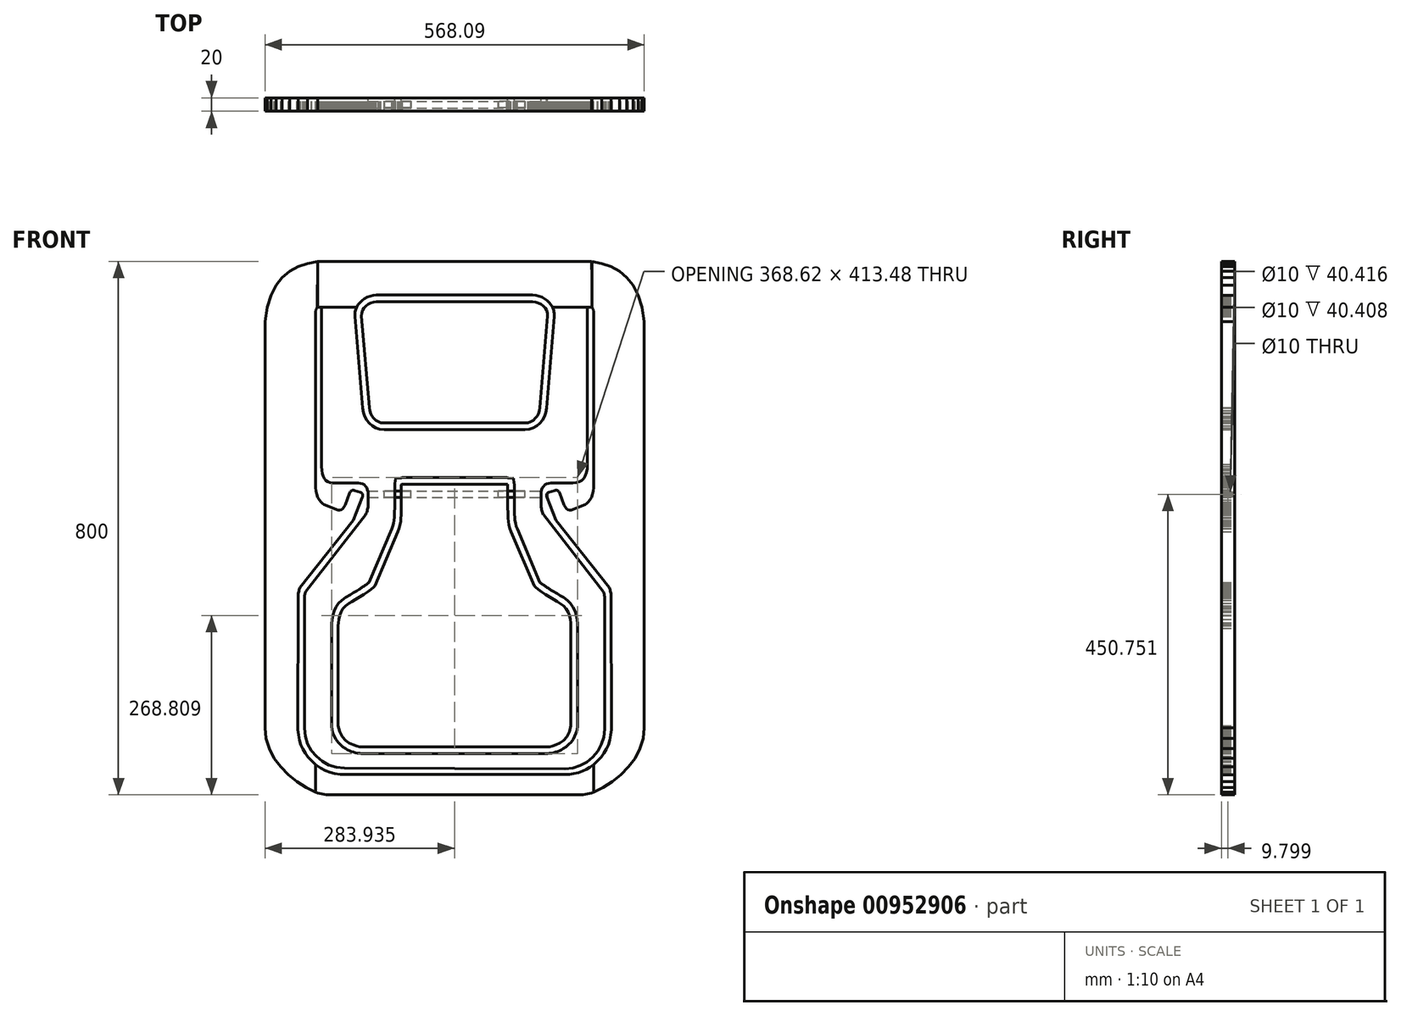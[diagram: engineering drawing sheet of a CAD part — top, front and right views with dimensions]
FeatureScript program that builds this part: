
annotation { "Feature Type Name" : "Feature", "Feature Type Description" : "" }
export const myFeature = defineFeature(function(context is Context, id is Id, definition is map)
    precondition{}
    {
        {
            var Q0;
            Q0=qCreatedBy(makeId("Front.planeOp"),FACE);
            var sketch = newSketch(context, id + "F0", { "sketchPlane" : qUnion([Q0])});
            skLineSegment(sketch, "E0", {"start": v(-236, -22.89) * mm, "end": v(-235.92, -20.82) * mm});
            skLineSegment(sketch, "E1", {"start": v(-235.92, -20.82) * mm, "end": v(-235.76, -18.83) * mm});
            skLineSegment(sketch, "E2", {"start": v(-235.76, -18.83) * mm, "end": v(-235.52, -16.92) * mm});
            skLineSegment(sketch, "E3", {"start": v(-235.52, -16.92) * mm, "end": v(-235.2, -15.08) * mm});
            skLineSegment(sketch, "E4", {"start": v(-235.2, -15.08) * mm, "end": v(-234.77, -13.32) * mm});
            skLineSegment(sketch, "E5", {"start": v(-234.77, -13.32) * mm, "end": v(-234.26, -11.64) * mm});
            skLineSegment(sketch, "E6", {"start": v(-234.26, -11.64) * mm, "end": v(-233.66, -10.04) * mm});
            skLineSegment(sketch, "E7", {"start": v(-233.66, -10.04) * mm, "end": v(-232.97, -8.51) * mm});
            skLineSegment(sketch, "E8", {"start": v(-232.97, -8.51) * mm, "end": v(-153.52, 92.53) * mm});
            skLineSegment(sketch, "E9", {"start": v(-153.52, 92.53) * mm, "end": v(-139.79, 126.67) * mm});
            skLineSegment(sketch, "E10", {"start": v(-139.79, 126.67) * mm, "end": v(-139.42, 128.13) * mm});
            skLineSegment(sketch, "E11", {"start": v(-139.42, 128.13) * mm, "end": v(-139.25, 129.45) * mm});
            skLineSegment(sketch, "E12", {"start": v(-139.25, 129.45) * mm, "end": v(-139.26, 130.64) * mm});
            skLineSegment(sketch, "E13", {"start": v(-139.26, 130.64) * mm, "end": v(-139.48, 131.68) * mm});
            skLineSegment(sketch, "E14", {"start": v(-139.48, 131.68) * mm, "end": v(-139.9, 132.57) * mm});
            skLineSegment(sketch, "E15", {"start": v(-139.9, 132.57) * mm, "end": v(-140.52, 133.3) * mm});
            skLineSegment(sketch, "E16", {"start": v(-140.52, 133.3) * mm, "end": v(-141.36, 133.9) * mm});
            skLineSegment(sketch, "E17", {"start": v(-141.36, 133.9) * mm, "end": v(-142.41, 134.32) * mm});
            skLineSegment(sketch, "E18", {"start": v(-142.41, 134.32) * mm, "end": v(-151.62, 137.29) * mm});
            skLineSegment(sketch, "E19", {"start": v(-151.62, 137.29) * mm, "end": v(-152.75, 137.59) * mm});
            skLineSegment(sketch, "E20", {"start": v(-152.75, 137.59) * mm, "end": v(-153.83, 137.65) * mm});
            skLineSegment(sketch, "E21", {"start": v(-153.83, 137.65) * mm, "end": v(-154.83, 137.49) * mm});
            skLineSegment(sketch, "E22", {"start": v(-154.83, 137.49) * mm, "end": v(-155.77, 137.09) * mm});
            skLineSegment(sketch, "E23", {"start": v(-155.77, 137.09) * mm, "end": v(-156.64, 136.46) * mm});
            skLineSegment(sketch, "E24", {"start": v(-156.64, 136.46) * mm, "end": v(-157.45, 135.6) * mm});
            skLineSegment(sketch, "E25", {"start": v(-157.45, 135.6) * mm, "end": v(-158.2, 134.51) * mm});
            skLineSegment(sketch, "E26", {"start": v(-158.2, 134.51) * mm, "end": v(-158.87, 133.2) * mm});
            skLineSegment(sketch, "E27", {"start": v(-158.87, 133.2) * mm, "end": v(-165.34, 115.81) * mm});
            skLineSegment(sketch, "E28", {"start": v(-165.34, 115.81) * mm, "end": v(-166.26, 113.6) * mm});
            skLineSegment(sketch, "E29", {"start": v(-166.26, 113.6) * mm, "end": v(-167.54, 111.66) * mm});
            skLineSegment(sketch, "E30", {"start": v(-167.54, 111.66) * mm, "end": v(-169.17, 110.05) * mm});
            skLineSegment(sketch, "E31", {"start": v(-169.17, 110.05) * mm, "end": v(-171.13, 108.84) * mm});
            skLineSegment(sketch, "E32", {"start": v(-171.13, 108.84) * mm, "end": v(-173.42, 108.07) * mm});
            skLineSegment(sketch, "E33", {"start": v(-173.42, 108.07) * mm, "end": v(-176.03, 107.8) * mm});
            skLineSegment(sketch, "E34", {"start": v(-176.03, 107.8) * mm, "end": v(-196.78, 116.12) * mm});
            skLineSegment(sketch, "E35", {"start": v(-196.78, 116.12) * mm, "end": v(-198.9, 117.6) * mm});
            skLineSegment(sketch, "E36", {"start": v(-198.9, 117.6) * mm, "end": v(-201.72, 119.68) * mm});
            skLineSegment(sketch, "E37", {"start": v(-201.72, 119.68) * mm, "end": v(-204.22, 122.87) * mm});
            skLineSegment(sketch, "E38", {"start": v(-204.22, 122.87) * mm, "end": v(-206.35, 126.93) * mm});
            skLineSegment(sketch, "E39", {"start": v(-206.35, 126.93) * mm, "end": v(-208.03, 131.6) * mm});
            skLineSegment(sketch, "E40", {"start": v(-208.03, 131.6) * mm, "end": v(-209.22, 136.65) * mm});
            skLineSegment(sketch, "E41", {"start": v(-209.22, 136.65) * mm, "end": v(-209.85, 141.84) * mm});
            skLineSegment(sketch, "E42", {"start": v(-209.85, 141.84) * mm, "end": v(-209.84, 146.93) * mm});
            skLineSegment(sketch, "E43", {"start": v(-209.84, 146.93) * mm, "end": v(-209.8, 404.8) * mm});
            skLineSegment(sketch, "E44", {"start": v(-209.8, 404.8) * mm, "end": v(-208.92, 409.14) * mm});
            skLineSegment(sketch, "E45", {"start": v(-208.92, 409.14) * mm, "end": v(-207.88, 411.04) * mm});
            skLineSegment(sketch, "E46", {"start": v(-207.88, 411.04) * mm, "end": v(-207.1, 412) * mm});
            skLineSegment(sketch, "E47", {"start": v(-207.1, 412) * mm, "end": v(-206.85, 480.96) * mm});
            skLineSegment(sketch, "E48", {"start": v(-206.85, 480.96) * mm, "end": v(-221.87, 477.75) * mm});
            skLineSegment(sketch, "E49", {"start": v(-221.87, 477.75) * mm, "end": v(-235.8, 472.86) * mm});
            skLineSegment(sketch, "E50", {"start": v(-235.8, 472.86) * mm, "end": v(-248.45, 465.95) * mm});
            skLineSegment(sketch, "E51", {"start": v(-248.45, 465.95) * mm, "end": v(-259.6, 456.72) * mm});
            skLineSegment(sketch, "E52", {"start": v(-259.6, 456.72) * mm, "end": v(-269.08, 444.86) * mm});
            skLineSegment(sketch, "E53", {"start": v(-269.08, 444.86) * mm, "end": v(-276.67, 430.05) * mm});
            skLineSegment(sketch, "E54", {"start": v(-276.67, 430.05) * mm, "end": v(-282.17, 411.98) * mm});
            skLineSegment(sketch, "E55", {"start": v(-282.17, 411.98) * mm, "end": v(-285.38, 390.33) * mm});
            skLineSegment(sketch, "E56", {"start": v(-285.38, 390.33) * mm, "end": v(-285.44, 100.9) * mm});
            skLineSegment(sketch, "E57", {"start": v(-285.44, 100.9) * mm, "end": v(-285.44, 77.3) * mm});
            skLineSegment(sketch, "E58", {"start": v(-285.44, 77.3) * mm, "end": v(-285.5, -218.16) * mm});
            skLineSegment(sketch, "E59", {"start": v(-285.5, -218.16) * mm, "end": v(-283.83, -234.28) * mm});
            skLineSegment(sketch, "E60", {"start": v(-283.83, -234.28) * mm, "end": v(-279.09, -249.58) * mm});
            skLineSegment(sketch, "E61", {"start": v(-279.09, -249.58) * mm, "end": v(-271.7, -263.88) * mm});
            skLineSegment(sketch, "E62", {"start": v(-271.7, -263.88) * mm, "end": v(-262.08, -277.04) * mm});
            skLineSegment(sketch, "E63", {"start": v(-262.08, -277.04) * mm, "end": v(-250.65, -288.89) * mm});
            skLineSegment(sketch, "E64", {"start": v(-250.65, -288.89) * mm, "end": v(-237.81, -299.27) * mm});
            skLineSegment(sketch, "E65", {"start": v(-237.81, -299.27) * mm, "end": v(-224, -308.03) * mm});
            skLineSegment(sketch, "E66", {"start": v(-224, -308.03) * mm, "end": v(-209.62, -315) * mm});
            skLineSegment(sketch, "E67", {"start": v(-209.62, -315) * mm, "end": v(-209.48, -273.95) * mm});
            skLineSegment(sketch, "E68", {"start": v(-209.48, -273.95) * mm, "end": v(-215.61, -268.18) * mm});
            skLineSegment(sketch, "E69", {"start": v(-215.61, -268.18) * mm, "end": v(-220.86, -262.44) * mm});
            skLineSegment(sketch, "E70", {"start": v(-220.86, -262.44) * mm, "end": v(-225.26, -256.6) * mm});
            skLineSegment(sketch, "E71", {"start": v(-225.26, -256.6) * mm, "end": v(-228.86, -250.52) * mm});
            skLineSegment(sketch, "E72", {"start": v(-228.86, -250.52) * mm, "end": v(-231.71, -244.04) * mm});
            skLineSegment(sketch, "E73", {"start": v(-231.71, -244.04) * mm, "end": v(-233.86, -237.03) * mm});
            skLineSegment(sketch, "E74", {"start": v(-233.86, -237.03) * mm, "end": v(-235.35, -229.35) * mm});
            skLineSegment(sketch, "E75", {"start": v(-235.35, -229.35) * mm, "end": v(-236.24, -220.86) * mm});
            skLineSegment(sketch, "E76", {"start": v(-236.24, -220.86) * mm, "end": v(-236, -22.89) * mm});
            skLineSegment(sketch, "E77", {"start": v(233.1, -22.89) * mm, "end": v(233.02, -20.82) * mm});
            skLineSegment(sketch, "E78", {"start": v(233.02, -20.82) * mm, "end": v(232.87, -18.83) * mm});
            skLineSegment(sketch, "E79", {"start": v(232.87, -18.83) * mm, "end": v(232.62, -16.92) * mm});
            skLineSegment(sketch, "E80", {"start": v(232.62, -16.92) * mm, "end": v(232.3, -15.08) * mm});
            skLineSegment(sketch, "E81", {"start": v(232.3, -15.08) * mm, "end": v(231.87, -13.32) * mm});
            skLineSegment(sketch, "E82", {"start": v(231.87, -13.32) * mm, "end": v(231.37, -11.64) * mm});
            skLineSegment(sketch, "E83", {"start": v(231.37, -11.64) * mm, "end": v(230.76, -10.04) * mm});
            skLineSegment(sketch, "E84", {"start": v(230.76, -10.04) * mm, "end": v(230.07, -8.51) * mm});
            skLineSegment(sketch, "E85", {"start": v(230.07, -8.51) * mm, "end": v(150.62, 92.53) * mm});
            skLineSegment(sketch, "E86", {"start": v(150.62, 92.53) * mm, "end": v(136.89, 126.67) * mm});
            skLineSegment(sketch, "E87", {"start": v(136.89, 126.67) * mm, "end": v(136.52, 128.13) * mm});
            skLineSegment(sketch, "E88", {"start": v(136.52, 128.13) * mm, "end": v(136.35, 129.45) * mm});
            skLineSegment(sketch, "E89", {"start": v(136.35, 129.45) * mm, "end": v(136.37, 130.64) * mm});
            skLineSegment(sketch, "E90", {"start": v(136.37, 130.64) * mm, "end": v(136.58, 131.68) * mm});
            skLineSegment(sketch, "E91", {"start": v(136.58, 131.68) * mm, "end": v(137, 132.57) * mm});
            skLineSegment(sketch, "E92", {"start": v(137, 132.57) * mm, "end": v(137.63, 133.3) * mm});
            skLineSegment(sketch, "E93", {"start": v(137.63, 133.3) * mm, "end": v(138.46, 133.9) * mm});
            skLineSegment(sketch, "E94", {"start": v(138.46, 133.9) * mm, "end": v(139.51, 134.32) * mm});
            skLineSegment(sketch, "E95", {"start": v(139.51, 134.32) * mm, "end": v(148.72, 137.29) * mm});
            skLineSegment(sketch, "E96", {"start": v(148.72, 137.29) * mm, "end": v(149.86, 137.59) * mm});
            skLineSegment(sketch, "E97", {"start": v(149.86, 137.59) * mm, "end": v(150.93, 137.65) * mm});
            skLineSegment(sketch, "E98", {"start": v(150.93, 137.65) * mm, "end": v(151.93, 137.49) * mm});
            skLineSegment(sketch, "E99", {"start": v(151.93, 137.49) * mm, "end": v(152.87, 137.09) * mm});
            skLineSegment(sketch, "E100", {"start": v(152.87, 137.09) * mm, "end": v(153.75, 136.46) * mm});
            skLineSegment(sketch, "E101", {"start": v(153.75, 136.46) * mm, "end": v(154.56, 135.6) * mm});
            skLineSegment(sketch, "E102", {"start": v(154.56, 135.6) * mm, "end": v(155.3, 134.51) * mm});
            skLineSegment(sketch, "E103", {"start": v(155.3, 134.51) * mm, "end": v(155.98, 133.2) * mm});
            skLineSegment(sketch, "E104", {"start": v(155.98, 133.2) * mm, "end": v(162.44, 115.81) * mm});
            skLineSegment(sketch, "E105", {"start": v(162.44, 115.81) * mm, "end": v(163.36, 113.6) * mm});
            skLineSegment(sketch, "E106", {"start": v(163.36, 113.6) * mm, "end": v(164.64, 111.66) * mm});
            skLineSegment(sketch, "E107", {"start": v(164.64, 111.66) * mm, "end": v(166.27, 110.05) * mm});
            skLineSegment(sketch, "E108", {"start": v(166.27, 110.05) * mm, "end": v(168.23, 108.84) * mm});
            skLineSegment(sketch, "E109", {"start": v(168.23, 108.84) * mm, "end": v(170.52, 108.07) * mm});
            skLineSegment(sketch, "E110", {"start": v(170.52, 108.07) * mm, "end": v(173.13, 107.8) * mm});
            skLineSegment(sketch, "E111", {"start": v(173.13, 107.8) * mm, "end": v(193.88, 116.12) * mm});
            skLineSegment(sketch, "E112", {"start": v(193.88, 116.12) * mm, "end": v(196, 117.6) * mm});
            skLineSegment(sketch, "E113", {"start": v(196, 117.6) * mm, "end": v(198.82, 119.68) * mm});
            skLineSegment(sketch, "E114", {"start": v(198.82, 119.68) * mm, "end": v(201.32, 122.87) * mm});
            skLineSegment(sketch, "E115", {"start": v(201.32, 122.87) * mm, "end": v(203.45, 126.93) * mm});
            skLineSegment(sketch, "E116", {"start": v(203.45, 126.93) * mm, "end": v(205.14, 131.6) * mm});
            skLineSegment(sketch, "E117", {"start": v(205.14, 131.6) * mm, "end": v(206.32, 136.65) * mm});
            skLineSegment(sketch, "E118", {"start": v(206.32, 136.65) * mm, "end": v(206.95, 141.84) * mm});
            skLineSegment(sketch, "E119", {"start": v(206.95, 141.84) * mm, "end": v(206.95, 146.93) * mm});
            skLineSegment(sketch, "E120", {"start": v(206.95, 146.93) * mm, "end": v(206.9, 404.8) * mm});
            skLineSegment(sketch, "E121", {"start": v(206.9, 404.8) * mm, "end": v(206.02, 409.14) * mm});
            skLineSegment(sketch, "E122", {"start": v(206.02, 409.14) * mm, "end": v(204.99, 411.04) * mm});
            skLineSegment(sketch, "E123", {"start": v(204.99, 411.04) * mm, "end": v(204.2, 412) * mm});
            skLineSegment(sketch, "E124", {"start": v(204.2, 412) * mm, "end": v(203.96, 480.96) * mm});
            skLineSegment(sketch, "E125", {"start": v(203.96, 480.96) * mm, "end": v(218.97, 477.75) * mm});
            skLineSegment(sketch, "E126", {"start": v(218.97, 477.75) * mm, "end": v(232.9, 472.86) * mm});
            skLineSegment(sketch, "E127", {"start": v(232.9, 472.86) * mm, "end": v(245.55, 465.95) * mm});
            skLineSegment(sketch, "E128", {"start": v(245.55, 465.95) * mm, "end": v(256.7, 456.72) * mm});
            skLineSegment(sketch, "E129", {"start": v(256.7, 456.72) * mm, "end": v(266.18, 444.86) * mm});
            skLineSegment(sketch, "E130", {"start": v(266.18, 444.86) * mm, "end": v(273.77, 430.05) * mm});
            skLineSegment(sketch, "E131", {"start": v(273.77, 430.05) * mm, "end": v(279.27, 411.98) * mm});
            skLineSegment(sketch, "E132", {"start": v(279.27, 411.98) * mm, "end": v(282.49, 390.33) * mm});
            skLineSegment(sketch, "E133", {"start": v(282.49, 390.33) * mm, "end": v(282.54, 100.9) * mm});
            skLineSegment(sketch, "E134", {"start": v(282.54, 100.9) * mm, "end": v(282.54, 77.3) * mm});
            skLineSegment(sketch, "E135", {"start": v(282.54, 77.3) * mm, "end": v(282.6, -218.16) * mm});
            skLineSegment(sketch, "E136", {"start": v(282.6, -218.16) * mm, "end": v(280.93, -234.28) * mm});
            skLineSegment(sketch, "E137", {"start": v(280.93, -234.28) * mm, "end": v(276.2, -249.58) * mm});
            skLineSegment(sketch, "E138", {"start": v(276.2, -249.58) * mm, "end": v(268.8, -263.88) * mm});
            skLineSegment(sketch, "E139", {"start": v(268.8, -263.88) * mm, "end": v(259.18, -277.04) * mm});
            skLineSegment(sketch, "E140", {"start": v(259.18, -277.04) * mm, "end": v(247.75, -288.89) * mm});
            skLineSegment(sketch, "E141", {"start": v(247.75, -288.89) * mm, "end": v(234.91, -299.27) * mm});
            skLineSegment(sketch, "E142", {"start": v(234.91, -299.27) * mm, "end": v(221.1, -308.03) * mm});
            skLineSegment(sketch, "E143", {"start": v(221.1, -308.03) * mm, "end": v(206.72, -315) * mm});
            skLineSegment(sketch, "E144", {"start": v(206.72, -315) * mm, "end": v(206.58, -273.95) * mm});
            skLineSegment(sketch, "E145", {"start": v(206.58, -273.95) * mm, "end": v(212.72, -268.18) * mm});
            skLineSegment(sketch, "E146", {"start": v(212.72, -268.18) * mm, "end": v(217.96, -262.44) * mm});
            skLineSegment(sketch, "E147", {"start": v(217.96, -262.44) * mm, "end": v(222.36, -256.6) * mm});
            skLineSegment(sketch, "E148", {"start": v(222.36, -256.6) * mm, "end": v(225.96, -250.52) * mm});
            skLineSegment(sketch, "E149", {"start": v(225.96, -250.52) * mm, "end": v(228.81, -244.04) * mm});
            skLineSegment(sketch, "E150", {"start": v(228.81, -244.04) * mm, "end": v(230.96, -237.03) * mm});
            skLineSegment(sketch, "E151", {"start": v(230.96, -237.03) * mm, "end": v(232.46, -229.35) * mm});
            skLineSegment(sketch, "E152", {"start": v(232.46, -229.35) * mm, "end": v(233.34, -220.86) * mm});
            skLineSegment(sketch, "E153", {"start": v(233.34, -220.86) * mm, "end": v(233.1, -22.89) * mm});
            skLineSegment(sketch, "E154", {"start": v(7370.2, 228.1) * mm, "end": v(7370.2, 231.56) * mm});
            skLineSegment(sketch, "E155", {"start": v(7370.2, 231.56) * mm, "end": v(7369.85, 231.56) * mm});
            skLineSegment(sketch, "E156", {"start": v(7369.85, 231.56) * mm, "end": v(7368.9, 230.83) * mm});
            skLineSegment(sketch, "E157", {"start": v(7368.9, 230.83) * mm, "end": v(7369.13, 230.55) * mm});
            skLineSegment(sketch, "E158", {"start": v(7369.13, 230.55) * mm, "end": v(7369.2, 230.6) * mm});
            skLineSegment(sketch, "E159", {"start": v(7369.2, 230.6) * mm, "end": v(7369.27, 230.66) * mm});
            skLineSegment(sketch, "E160", {"start": v(7369.27, 230.66) * mm, "end": v(7369.34, 230.72) * mm});
            skLineSegment(sketch, "E161", {"start": v(7369.34, 230.72) * mm, "end": v(7369.4, 230.77) * mm});
            skLineSegment(sketch, "E162", {"start": v(7369.4, 230.77) * mm, "end": v(7369.47, 230.83) * mm});
            skLineSegment(sketch, "E163", {"start": v(7369.47, 230.83) * mm, "end": v(7369.53, 230.88) * mm});
            skLineSegment(sketch, "E164", {"start": v(7369.53, 230.88) * mm, "end": v(7369.6, 230.93) * mm});
            skLineSegment(sketch, "E165", {"start": v(7369.6, 230.93) * mm, "end": v(7369.66, 230.98) * mm});
            skLineSegment(sketch, "E166", {"start": v(7369.66, 230.98) * mm, "end": v(7369.7, 231.01) * mm});
            skLineSegment(sketch, "E167", {"start": v(7369.7, 231.01) * mm, "end": v(7369.73, 231.05) * mm});
            skLineSegment(sketch, "E168", {"start": v(7369.73, 231.05) * mm, "end": v(7369.77, 231.08) * mm});
            skLineSegment(sketch, "E169", {"start": v(7369.77, 231.08) * mm, "end": v(7369.8, 231.12) * mm});
            skLineSegment(sketch, "E170", {"start": v(7369.8, 231.12) * mm, "end": v(7369.8, 231.05) * mm});
            skLineSegment(sketch, "E171", {"start": v(7369.8, 231.05) * mm, "end": v(7369.8, 230.98) * mm});
            skLineSegment(sketch, "E172", {"start": v(7369.8, 230.98) * mm, "end": v(7369.79, 230.9) * mm});
            skLineSegment(sketch, "E173", {"start": v(7369.79, 230.9) * mm, "end": v(7369.79, 230.83) * mm});
            skLineSegment(sketch, "E174", {"start": v(7369.79, 230.83) * mm, "end": v(7369.78, 230.75) * mm});
            skLineSegment(sketch, "E175", {"start": v(7369.78, 230.75) * mm, "end": v(7369.78, 230.68) * mm});
            skLineSegment(sketch, "E176", {"start": v(7369.78, 230.68) * mm, "end": v(7369.78, 230.6) * mm});
            skLineSegment(sketch, "E177", {"start": v(7369.78, 230.6) * mm, "end": v(7369.78, 230.52) * mm});
            skLineSegment(sketch, "E178", {"start": v(7369.78, 230.52) * mm, "end": v(7369.78, 228.1) * mm});
            skLineSegment(sketch, "E179", {"start": v(7369.78, 228.1) * mm, "end": v(7370.2, 228.1) * mm});
            skLineSegment(sketch, "E180", {"start": v(7371.6, 230.44) * mm, "end": v(7371.6, 230.4) * mm});
            skLineSegment(sketch, "E181", {"start": v(7371.6, 230.4) * mm, "end": v(7371.6, 230.36) * mm});
            skLineSegment(sketch, "E182", {"start": v(7371.6, 230.36) * mm, "end": v(7371.61, 230.33) * mm});
            skLineSegment(sketch, "E183", {"start": v(7371.61, 230.33) * mm, "end": v(7371.62, 230.3) * mm});
            skLineSegment(sketch, "E184", {"start": v(7371.62, 230.3) * mm, "end": v(7371.63, 230.27) * mm});
            skLineSegment(sketch, "E185", {"start": v(7371.63, 230.27) * mm, "end": v(7371.64, 230.24) * mm});
            skLineSegment(sketch, "E186", {"start": v(7371.64, 230.24) * mm, "end": v(7371.66, 230.22) * mm});
            skLineSegment(sketch, "E187", {"start": v(7371.66, 230.22) * mm, "end": v(7371.68, 230.2) * mm});
            skLineSegment(sketch, "E188", {"start": v(7371.68, 230.2) * mm, "end": v(7371.7, 230.17) * mm});
            skLineSegment(sketch, "E189", {"start": v(7371.7, 230.17) * mm, "end": v(7371.72, 230.15) * mm});
            skLineSegment(sketch, "E190", {"start": v(7371.72, 230.15) * mm, "end": v(7371.75, 230.14) * mm});
            skLineSegment(sketch, "E191", {"start": v(7371.75, 230.14) * mm, "end": v(7371.77, 230.13) * mm});
            skLineSegment(sketch, "E192", {"start": v(7371.77, 230.13) * mm, "end": v(7371.8, 230.12) * mm});
            skLineSegment(sketch, "E193", {"start": v(7371.8, 230.12) * mm, "end": v(7371.83, 230.11) * mm});
            skLineSegment(sketch, "E194", {"start": v(7371.83, 230.11) * mm, "end": v(7371.86, 230.1) * mm});
            skLineSegment(sketch, "E195", {"start": v(7371.86, 230.1) * mm, "end": v(7371.9, 230.1) * mm});
            skLineSegment(sketch, "E196", {"start": v(7371.9, 230.1) * mm, "end": v(7371.93, 230.1) * mm});
            skLineSegment(sketch, "E197", {"start": v(7371.93, 230.1) * mm, "end": v(7371.97, 230.11) * mm});
            skLineSegment(sketch, "E198", {"start": v(7371.97, 230.11) * mm, "end": v(7372, 230.12) * mm});
            skLineSegment(sketch, "E199", {"start": v(7372, 230.12) * mm, "end": v(7372.03, 230.13) * mm});
            skLineSegment(sketch, "E200", {"start": v(7372.03, 230.13) * mm, "end": v(7372.05, 230.14) * mm});
            skLineSegment(sketch, "E201", {"start": v(7372.05, 230.14) * mm, "end": v(7372.08, 230.15) * mm});
            skLineSegment(sketch, "E202", {"start": v(7372.08, 230.15) * mm, "end": v(7372.1, 230.17) * mm});
            skLineSegment(sketch, "E203", {"start": v(7372.1, 230.17) * mm, "end": v(7372.12, 230.2) * mm});
            skLineSegment(sketch, "E204", {"start": v(7372.12, 230.2) * mm, "end": v(7372.14, 230.22) * mm});
            skLineSegment(sketch, "E205", {"start": v(7372.14, 230.22) * mm, "end": v(7372.16, 230.24) * mm});
            skLineSegment(sketch, "E206", {"start": v(7372.16, 230.24) * mm, "end": v(7372.17, 230.27) * mm});
            skLineSegment(sketch, "E207", {"start": v(7372.17, 230.27) * mm, "end": v(7372.18, 230.3) * mm});
            skLineSegment(sketch, "E208", {"start": v(7372.18, 230.3) * mm, "end": v(7372.2, 230.33) * mm});
            skLineSegment(sketch, "E209", {"start": v(7372.2, 230.33) * mm, "end": v(7372.2, 230.36) * mm});
            skLineSegment(sketch, "E210", {"start": v(7372.2, 230.36) * mm, "end": v(7372.2, 230.4) * mm});
            skLineSegment(sketch, "E211", {"start": v(7372.2, 230.4) * mm, "end": v(7372.2, 230.44) * mm});
            skLineSegment(sketch, "E212", {"start": v(7372.2, 230.44) * mm, "end": v(7372.2, 230.47) * mm});
            skLineSegment(sketch, "E213", {"start": v(7372.2, 230.47) * mm, "end": v(7372.2, 230.5) * mm});
            skLineSegment(sketch, "E214", {"start": v(7372.2, 230.5) * mm, "end": v(7372.2, 230.54) * mm});
            skLineSegment(sketch, "E215", {"start": v(7372.2, 230.54) * mm, "end": v(7372.18, 230.57) * mm});
            skLineSegment(sketch, "E216", {"start": v(7372.18, 230.57) * mm, "end": v(7372.17, 230.6) * mm});
            skLineSegment(sketch, "E217", {"start": v(7372.17, 230.6) * mm, "end": v(7372.16, 230.63) * mm});
            skLineSegment(sketch, "E218", {"start": v(7372.16, 230.63) * mm, "end": v(7372.14, 230.66) * mm});
            skLineSegment(sketch, "E219", {"start": v(7372.14, 230.66) * mm, "end": v(7372.13, 230.68) * mm});
            skLineSegment(sketch, "E220", {"start": v(7372.13, 230.68) * mm, "end": v(7372.1, 230.7) * mm});
            skLineSegment(sketch, "E221", {"start": v(7372.1, 230.7) * mm, "end": v(7372.08, 230.72) * mm});
            skLineSegment(sketch, "E222", {"start": v(7372.08, 230.72) * mm, "end": v(7372.06, 230.73) * mm});
            skLineSegment(sketch, "E223", {"start": v(7372.06, 230.73) * mm, "end": v(7372.03, 230.74) * mm});
            skLineSegment(sketch, "E224", {"start": v(7372.03, 230.74) * mm, "end": v(7372, 230.75) * mm});
            skLineSegment(sketch, "E225", {"start": v(7372, 230.75) * mm, "end": v(7371.97, 230.76) * mm});
            skLineSegment(sketch, "E226", {"start": v(7371.97, 230.76) * mm, "end": v(7371.93, 230.76) * mm});
            skLineSegment(sketch, "E227", {"start": v(7371.93, 230.76) * mm, "end": v(7371.9, 230.76) * mm});
            skLineSegment(sketch, "E228", {"start": v(7371.9, 230.76) * mm, "end": v(7371.86, 230.76) * mm});
            skLineSegment(sketch, "E229", {"start": v(7371.86, 230.76) * mm, "end": v(7371.83, 230.76) * mm});
            skLineSegment(sketch, "E230", {"start": v(7371.83, 230.76) * mm, "end": v(7371.8, 230.75) * mm});
            skLineSegment(sketch, "E231", {"start": v(7371.8, 230.75) * mm, "end": v(7371.77, 230.74) * mm});
            skLineSegment(sketch, "E232", {"start": v(7371.77, 230.74) * mm, "end": v(7371.74, 230.73) * mm});
            skLineSegment(sketch, "E233", {"start": v(7371.74, 230.73) * mm, "end": v(7371.72, 230.71) * mm});
            skLineSegment(sketch, "E234", {"start": v(7371.72, 230.71) * mm, "end": v(7371.7, 230.7) * mm});
            skLineSegment(sketch, "E235", {"start": v(7371.7, 230.7) * mm, "end": v(7371.67, 230.68) * mm});
            skLineSegment(sketch, "E236", {"start": v(7371.67, 230.68) * mm, "end": v(7371.66, 230.65) * mm});
            skLineSegment(sketch, "E237", {"start": v(7371.66, 230.65) * mm, "end": v(7371.64, 230.63) * mm});
            skLineSegment(sketch, "E238", {"start": v(7371.64, 230.63) * mm, "end": v(7371.63, 230.6) * mm});
            skLineSegment(sketch, "E239", {"start": v(7371.63, 230.6) * mm, "end": v(7371.62, 230.57) * mm});
            skLineSegment(sketch, "E240", {"start": v(7371.62, 230.57) * mm, "end": v(7371.61, 230.54) * mm});
            skLineSegment(sketch, "E241", {"start": v(7371.61, 230.54) * mm, "end": v(7371.6, 230.5) * mm});
            skLineSegment(sketch, "E242", {"start": v(7371.6, 230.5) * mm, "end": v(7371.6, 230.47) * mm});
            skLineSegment(sketch, "E243", {"start": v(7371.6, 230.47) * mm, "end": v(7371.6, 230.44) * mm});
            skLineSegment(sketch, "E244", {"start": v(7371.6, 228.36) * mm, "end": v(7371.6, 228.32) * mm});
            skLineSegment(sketch, "E245", {"start": v(7371.6, 228.32) * mm, "end": v(7371.6, 228.28) * mm});
            skLineSegment(sketch, "E246", {"start": v(7371.6, 228.28) * mm, "end": v(7371.61, 228.25) * mm});
            skLineSegment(sketch, "E247", {"start": v(7371.61, 228.25) * mm, "end": v(7371.62, 228.22) * mm});
            skLineSegment(sketch, "E248", {"start": v(7371.62, 228.22) * mm, "end": v(7371.63, 228.19) * mm});
            skLineSegment(sketch, "E249", {"start": v(7371.63, 228.19) * mm, "end": v(7371.64, 228.16) * mm});
            skLineSegment(sketch, "E250", {"start": v(7371.64, 228.16) * mm, "end": v(7371.66, 228.14) * mm});
            skLineSegment(sketch, "E251", {"start": v(7371.66, 228.14) * mm, "end": v(7371.68, 228.11) * mm});
            skLineSegment(sketch, "E252", {"start": v(7371.68, 228.11) * mm, "end": v(7371.7, 228.1) * mm});
            skLineSegment(sketch, "E253", {"start": v(7371.7, 228.1) * mm, "end": v(7371.72, 228.08) * mm});
            skLineSegment(sketch, "E254", {"start": v(7371.72, 228.08) * mm, "end": v(7371.75, 228.06) * mm});
            skLineSegment(sketch, "E255", {"start": v(7371.75, 228.06) * mm, "end": v(7371.77, 228.05) * mm});
            skLineSegment(sketch, "E256", {"start": v(7371.77, 228.05) * mm, "end": v(7371.8, 228.04) * mm});
            skLineSegment(sketch, "E257", {"start": v(7371.8, 228.04) * mm, "end": v(7371.83, 228.03) * mm});
            skLineSegment(sketch, "E258", {"start": v(7371.83, 228.03) * mm, "end": v(7371.86, 228.03) * mm});
            skLineSegment(sketch, "E259", {"start": v(7371.86, 228.03) * mm, "end": v(7371.9, 228.02) * mm});
            skLineSegment(sketch, "E260", {"start": v(7371.9, 228.02) * mm, "end": v(7371.93, 228.03) * mm});
            skLineSegment(sketch, "E261", {"start": v(7371.93, 228.03) * mm, "end": v(7371.97, 228.03) * mm});
            skLineSegment(sketch, "E262", {"start": v(7371.97, 228.03) * mm, "end": v(7372, 228.04) * mm});
            skLineSegment(sketch, "E263", {"start": v(7372, 228.04) * mm, "end": v(7372.03, 228.05) * mm});
            skLineSegment(sketch, "E264", {"start": v(7372.03, 228.05) * mm, "end": v(7372.05, 228.06) * mm});
            skLineSegment(sketch, "E265", {"start": v(7372.05, 228.06) * mm, "end": v(7372.08, 228.08) * mm});
            skLineSegment(sketch, "E266", {"start": v(7372.08, 228.08) * mm, "end": v(7372.1, 228.1) * mm});
            skLineSegment(sketch, "E267", {"start": v(7372.1, 228.1) * mm, "end": v(7372.12, 228.11) * mm});
            skLineSegment(sketch, "E268", {"start": v(7372.12, 228.11) * mm, "end": v(7372.14, 228.14) * mm});
            skLineSegment(sketch, "E269", {"start": v(7372.14, 228.14) * mm, "end": v(7372.16, 228.16) * mm});
            skLineSegment(sketch, "E270", {"start": v(7372.16, 228.16) * mm, "end": v(7372.17, 228.19) * mm});
            skLineSegment(sketch, "E271", {"start": v(7372.17, 228.19) * mm, "end": v(7372.18, 228.22) * mm});
            skLineSegment(sketch, "E272", {"start": v(7372.18, 228.22) * mm, "end": v(7372.2, 228.25) * mm});
            skLineSegment(sketch, "E273", {"start": v(7372.2, 228.25) * mm, "end": v(7372.2, 228.28) * mm});
            skLineSegment(sketch, "E274", {"start": v(7372.2, 228.28) * mm, "end": v(7372.2, 228.32) * mm});
            skLineSegment(sketch, "E275", {"start": v(7372.2, 228.32) * mm, "end": v(7372.2, 228.36) * mm});
            skLineSegment(sketch, "E276", {"start": v(7372.2, 228.36) * mm, "end": v(7372.2, 228.4) * mm});
            skLineSegment(sketch, "E277", {"start": v(7372.2, 228.4) * mm, "end": v(7372.2, 228.43) * mm});
            skLineSegment(sketch, "E278", {"start": v(7372.2, 228.43) * mm, "end": v(7372.2, 228.46) * mm});
            skLineSegment(sketch, "E279", {"start": v(7372.2, 228.46) * mm, "end": v(7372.18, 228.5) * mm});
            skLineSegment(sketch, "E280", {"start": v(7372.18, 228.5) * mm, "end": v(7372.17, 228.52) * mm});
            skLineSegment(sketch, "E281", {"start": v(7372.17, 228.52) * mm, "end": v(7372.16, 228.55) * mm});
            skLineSegment(sketch, "E282", {"start": v(7372.16, 228.55) * mm, "end": v(7372.14, 228.57) * mm});
            skLineSegment(sketch, "E283", {"start": v(7372.14, 228.57) * mm, "end": v(7372.12, 228.6) * mm});
            skLineSegment(sketch, "E284", {"start": v(7372.12, 228.6) * mm, "end": v(7372.1, 228.62) * mm});
            skLineSegment(sketch, "E285", {"start": v(7372.1, 228.62) * mm, "end": v(7372.08, 228.63) * mm});
            skLineSegment(sketch, "E286", {"start": v(7372.08, 228.63) * mm, "end": v(7372.05, 228.65) * mm});
            skLineSegment(sketch, "E287", {"start": v(7372.05, 228.65) * mm, "end": v(7372.03, 228.66) * mm});
            skLineSegment(sketch, "E288", {"start": v(7372.03, 228.66) * mm, "end": v(7372, 228.67) * mm});
            skLineSegment(sketch, "E289", {"start": v(7372, 228.67) * mm, "end": v(7371.97, 228.68) * mm});
            skLineSegment(sketch, "E290", {"start": v(7371.97, 228.68) * mm, "end": v(7371.93, 228.68) * mm});
            skLineSegment(sketch, "E291", {"start": v(7371.93, 228.68) * mm, "end": v(7371.9, 228.68) * mm});
            skLineSegment(sketch, "E292", {"start": v(7371.9, 228.68) * mm, "end": v(7371.86, 228.68) * mm});
            skLineSegment(sketch, "E293", {"start": v(7371.86, 228.68) * mm, "end": v(7371.83, 228.68) * mm});
            skLineSegment(sketch, "E294", {"start": v(7371.83, 228.68) * mm, "end": v(7371.8, 228.67) * mm});
            skLineSegment(sketch, "E295", {"start": v(7371.8, 228.67) * mm, "end": v(7371.77, 228.66) * mm});
            skLineSegment(sketch, "E296", {"start": v(7371.77, 228.66) * mm, "end": v(7371.74, 228.65) * mm});
            skLineSegment(sketch, "E297", {"start": v(7371.74, 228.65) * mm, "end": v(7371.72, 228.63) * mm});
            skLineSegment(sketch, "E298", {"start": v(7371.72, 228.63) * mm, "end": v(7371.7, 228.62) * mm});
            skLineSegment(sketch, "E299", {"start": v(7371.7, 228.62) * mm, "end": v(7371.68, 228.6) * mm});
            skLineSegment(sketch, "E300", {"start": v(7371.68, 228.6) * mm, "end": v(7371.66, 228.57) * mm});
            skLineSegment(sketch, "E301", {"start": v(7371.66, 228.57) * mm, "end": v(7371.64, 228.55) * mm});
            skLineSegment(sketch, "E302", {"start": v(7371.64, 228.55) * mm, "end": v(7371.63, 228.52) * mm});
            skLineSegment(sketch, "E303", {"start": v(7371.63, 228.52) * mm, "end": v(7371.62, 228.5) * mm});
            skLineSegment(sketch, "E304", {"start": v(7371.62, 228.5) * mm, "end": v(7371.61, 228.46) * mm});
            skLineSegment(sketch, "E305", {"start": v(7371.61, 228.46) * mm, "end": v(7371.6, 228.43) * mm});
            skLineSegment(sketch, "E306", {"start": v(7371.6, 228.43) * mm, "end": v(7371.6, 228.4) * mm});
            skLineSegment(sketch, "E307", {"start": v(7371.6, 228.4) * mm, "end": v(7371.6, 228.36) * mm});
            skLineSegment(sketch, "E308", {"start": v(7374.28, 228.1) * mm, "end": v(7374.28, 231.56) * mm});
            skLineSegment(sketch, "E309", {"start": v(7374.28, 231.56) * mm, "end": v(7373.93, 231.56) * mm});
            skLineSegment(sketch, "E310", {"start": v(7373.93, 231.56) * mm, "end": v(7372.99, 230.83) * mm});
            skLineSegment(sketch, "E311", {"start": v(7372.99, 230.83) * mm, "end": v(7373.2, 230.55) * mm});
            skLineSegment(sketch, "E312", {"start": v(7373.2, 230.55) * mm, "end": v(7373.28, 230.6) * mm});
            skLineSegment(sketch, "E313", {"start": v(7373.28, 230.6) * mm, "end": v(7373.35, 230.66) * mm});
            skLineSegment(sketch, "E314", {"start": v(7373.35, 230.66) * mm, "end": v(7373.42, 230.72) * mm});
            skLineSegment(sketch, "E315", {"start": v(7373.42, 230.72) * mm, "end": v(7373.48, 230.77) * mm});
            skLineSegment(sketch, "E316", {"start": v(7373.48, 230.77) * mm, "end": v(7373.55, 230.83) * mm});
            skLineSegment(sketch, "E317", {"start": v(7373.55, 230.83) * mm, "end": v(7373.61, 230.88) * mm});
            skLineSegment(sketch, "E318", {"start": v(7373.61, 230.88) * mm, "end": v(7373.68, 230.93) * mm});
            skLineSegment(sketch, "E319", {"start": v(7373.68, 230.93) * mm, "end": v(7373.74, 230.98) * mm});
            skLineSegment(sketch, "E320", {"start": v(7373.74, 230.98) * mm, "end": v(7373.78, 231.01) * mm});
            skLineSegment(sketch, "E321", {"start": v(7373.78, 231.01) * mm, "end": v(7373.81, 231.05) * mm});
            skLineSegment(sketch, "E322", {"start": v(7373.81, 231.05) * mm, "end": v(7373.85, 231.08) * mm});
            skLineSegment(sketch, "E323", {"start": v(7373.85, 231.08) * mm, "end": v(7373.88, 231.12) * mm});
            skLineSegment(sketch, "E324", {"start": v(7373.88, 231.12) * mm, "end": v(7373.88, 231.05) * mm});
            skLineSegment(sketch, "E325", {"start": v(7373.88, 231.05) * mm, "end": v(7373.87, 230.98) * mm});
            skLineSegment(sketch, "E326", {"start": v(7373.87, 230.98) * mm, "end": v(7373.87, 230.9) * mm});
            skLineSegment(sketch, "E327", {"start": v(7373.87, 230.9) * mm, "end": v(7373.87, 230.83) * mm});
            skLineSegment(sketch, "E328", {"start": v(7373.87, 230.83) * mm, "end": v(7373.86, 230.75) * mm});
            skLineSegment(sketch, "E329", {"start": v(7373.86, 230.75) * mm, "end": v(7373.86, 230.68) * mm});
            skLineSegment(sketch, "E330", {"start": v(7373.86, 230.68) * mm, "end": v(7373.86, 230.6) * mm});
            skLineSegment(sketch, "E331", {"start": v(7373.86, 230.6) * mm, "end": v(7373.86, 230.52) * mm});
            skLineSegment(sketch, "E332", {"start": v(7373.86, 230.52) * mm, "end": v(7373.86, 228.1) * mm});
            skLineSegment(sketch, "E333", {"start": v(7373.86, 228.1) * mm, "end": v(7374.28, 228.1) * mm});
            skLineSegment(sketch, "E334", {"start": v(223.22, -24.14) * mm, "end": v(223.18, -22.93) * mm});
            skLineSegment(sketch, "E335", {"start": v(223.18, -22.93) * mm, "end": v(223.1, -21.7) * mm});
            skLineSegment(sketch, "E336", {"start": v(223.1, -21.7) * mm, "end": v(222.98, -20.45) * mm});
            skLineSegment(sketch, "E337", {"start": v(222.98, -20.45) * mm, "end": v(222.8, -19.2) * mm});
            skLineSegment(sketch, "E338", {"start": v(222.8, -19.2) * mm, "end": v(222.55, -17.97) * mm});
            skLineSegment(sketch, "E339", {"start": v(222.55, -17.97) * mm, "end": v(222.24, -16.76) * mm});
            skLineSegment(sketch, "E340", {"start": v(222.24, -16.76) * mm, "end": v(221.84, -15.59) * mm});
            skLineSegment(sketch, "E341", {"start": v(221.84, -15.59) * mm, "end": v(221.37, -14.47) * mm});
            skLineSegment(sketch, "E342", {"start": v(221.37, -14.47) * mm, "end": v(131.71, 100.66) * mm});
            skLineSegment(sketch, "E343", {"start": v(131.71, 100.66) * mm, "end": v(131.58, 100.95) * mm});
            skLineSegment(sketch, "E344", {"start": v(131.58, 100.95) * mm, "end": v(130.75, 102.8) * mm});
            skLineSegment(sketch, "E345", {"start": v(130.75, 102.8) * mm, "end": v(130.03, 104.7) * mm});
            skLineSegment(sketch, "E346", {"start": v(130.03, 104.7) * mm, "end": v(129.42, 106.61) * mm});
            skLineSegment(sketch, "E347", {"start": v(129.42, 106.61) * mm, "end": v(128.9, 108.56) * mm});
            skLineSegment(sketch, "E348", {"start": v(128.9, 108.56) * mm, "end": v(128.5, 110.52) * mm});
            skLineSegment(sketch, "E349", {"start": v(128.5, 110.52) * mm, "end": v(128.17, 112.51) * mm});
            skLineSegment(sketch, "E350", {"start": v(128.17, 112.51) * mm, "end": v(127.95, 114.52) * mm});
            skLineSegment(sketch, "E351", {"start": v(127.95, 114.52) * mm, "end": v(127.82, 116.55) * mm});
            skLineSegment(sketch, "E352", {"start": v(127.82, 116.55) * mm, "end": v(127.8, 116.76) * mm});
            skLineSegment(sketch, "E353", {"start": v(127.8, 116.76) * mm, "end": v(127.8, 132.18) * mm});
            skLineSegment(sketch, "E354", {"start": v(127.8, 132.18) * mm, "end": v(127.8, 132.28) * mm});
            skLineSegment(sketch, "E355", {"start": v(127.8, 132.28) * mm, "end": v(128.11, 135.53) * mm});
            skLineSegment(sketch, "E356", {"start": v(128.11, 135.53) * mm, "end": v(128.88, 138.56) * mm});
            skLineSegment(sketch, "E357", {"start": v(128.88, 138.56) * mm, "end": v(130.1, 141.32) * mm});
            skLineSegment(sketch, "E358", {"start": v(130.1, 141.32) * mm, "end": v(131.75, 143.73) * mm});
            skLineSegment(sketch, "E359", {"start": v(131.75, 143.73) * mm, "end": v(133.84, 145.71) * mm});
            skLineSegment(sketch, "E360", {"start": v(133.84, 145.71) * mm, "end": v(136.36, 147.2) * mm});
            skLineSegment(sketch, "E361", {"start": v(136.36, 147.2) * mm, "end": v(139.3, 148.13) * mm});
            skLineSegment(sketch, "E362", {"start": v(139.3, 148.13) * mm, "end": v(142.63, 148.43) * mm});
            skLineSegment(sketch, "E363", {"start": v(142.63, 148.43) * mm, "end": v(152, 148.43) * mm});
            skLineSegment(sketch, "E364", {"start": v(152, 148.43) * mm, "end": v(176.03, 148.43) * mm});
            skLineSegment(sketch, "E365", {"start": v(176.03, 148.43) * mm, "end": v(181.05, 148.94) * mm});
            skLineSegment(sketch, "E366", {"start": v(181.05, 148.94) * mm, "end": v(185.38, 150.34) * mm});
            skLineSegment(sketch, "E367", {"start": v(185.38, 150.34) * mm, "end": v(189.03, 152.6) * mm});
            skLineSegment(sketch, "E368", {"start": v(189.03, 152.6) * mm, "end": v(192.01, 155.7) * mm});
            skLineSegment(sketch, "E369", {"start": v(192.01, 155.7) * mm, "end": v(194.33, 159.64) * mm});
            skLineSegment(sketch, "E370", {"start": v(194.33, 159.64) * mm, "end": v(196, 164.4) * mm});
            skLineSegment(sketch, "E371", {"start": v(196, 164.4) * mm, "end": v(197.05, 169.96) * mm});
            skLineSegment(sketch, "E372", {"start": v(197.05, 169.96) * mm, "end": v(197.46, 176.31) * mm});
            skLineSegment(sketch, "E373", {"start": v(197.46, 176.31) * mm, "end": v(197.46, 410.78) * mm});
            skLineSegment(sketch, "E374", {"start": v(197.46, 410.78) * mm, "end": v(197.44, 411) * mm});
            skLineSegment(sketch, "E375", {"start": v(197.44, 411) * mm, "end": v(197.37, 411.2) * mm});
            skLineSegment(sketch, "E376", {"start": v(197.37, 411.2) * mm, "end": v(197.27, 411.38) * mm});
            skLineSegment(sketch, "E377", {"start": v(197.27, 411.38) * mm, "end": v(197.13, 411.54) * mm});
            skLineSegment(sketch, "E378", {"start": v(197.13, 411.54) * mm, "end": v(197.14, 411.56) * mm});
            skLineSegment(sketch, "E379", {"start": v(197.14, 411.56) * mm, "end": v(196.6, 411.72) * mm});
            skLineSegment(sketch, "E380", {"start": v(196.6, 411.72) * mm, "end": v(196.37, 411.74) * mm});
            skLineSegment(sketch, "E381", {"start": v(196.37, 411.74) * mm, "end": v(145.21, 411.86) * mm});
            skLineSegment(sketch, "E382", {"start": v(145.21, 411.86) * mm, "end": v(145.9, 410.28) * mm});
            skLineSegment(sketch, "E383", {"start": v(145.9, 410.28) * mm, "end": v(146.48, 408.64) * mm});
            skLineSegment(sketch, "E384", {"start": v(146.48, 408.64) * mm, "end": v(146.97, 406.97) * mm});
            skLineSegment(sketch, "E385", {"start": v(146.97, 406.97) * mm, "end": v(147.34, 405.26) * mm});
            skLineSegment(sketch, "E386", {"start": v(147.34, 405.26) * mm, "end": v(147.6, 403.51) * mm});
            skLineSegment(sketch, "E387", {"start": v(147.6, 403.51) * mm, "end": v(147.76, 401.73) * mm});
            skLineSegment(sketch, "E388", {"start": v(147.76, 401.73) * mm, "end": v(147.8, 399.93) * mm});
            skLineSegment(sketch, "E389", {"start": v(147.8, 399.93) * mm, "end": v(147.7, 398.1) * mm});
            skLineSegment(sketch, "E390", {"start": v(147.7, 398.1) * mm, "end": v(136.11, 260.66) * mm});
            skLineSegment(sketch, "E391", {"start": v(136.11, 260.66) * mm, "end": v(135.03, 254.23) * mm});
            skLineSegment(sketch, "E392", {"start": v(135.03, 254.23) * mm, "end": v(132.95, 248.22) * mm});
            skLineSegment(sketch, "E393", {"start": v(132.95, 248.22) * mm, "end": v(129.96, 242.76) * mm});
            skLineSegment(sketch, "E394", {"start": v(129.96, 242.76) * mm, "end": v(126.12, 238) * mm});
            skLineSegment(sketch, "E395", {"start": v(126.12, 238) * mm, "end": v(121.53, 234.06) * mm});
            skLineSegment(sketch, "E396", {"start": v(121.53, 234.06) * mm, "end": v(116.26, 231.09) * mm});
            skLineSegment(sketch, "E397", {"start": v(116.26, 231.09) * mm, "end": v(110.39, 229.2) * mm});
            skLineSegment(sketch, "E398", {"start": v(110.39, 229.2) * mm, "end": v(104, 228.54) * mm});
            skLineSegment(sketch, "E399", {"start": v(104, 228.54) * mm, "end": v(-107.12, 228.54) * mm});
            skLineSegment(sketch, "E400", {"start": v(-107.12, 228.54) * mm, "end": v(-113.5, 229.2) * mm});
            skLineSegment(sketch, "E401", {"start": v(-113.5, 229.2) * mm, "end": v(-119.38, 231.09) * mm});
            skLineSegment(sketch, "E402", {"start": v(-119.38, 231.09) * mm, "end": v(-124.65, 234.06) * mm});
            skLineSegment(sketch, "E403", {"start": v(-124.65, 234.06) * mm, "end": v(-129.24, 238) * mm});
            skLineSegment(sketch, "E404", {"start": v(-129.24, 238) * mm, "end": v(-133.08, 242.76) * mm});
            skLineSegment(sketch, "E405", {"start": v(-133.08, 242.76) * mm, "end": v(-136.08, 248.22) * mm});
            skLineSegment(sketch, "E406", {"start": v(-136.08, 248.22) * mm, "end": v(-138.15, 254.23) * mm});
            skLineSegment(sketch, "E407", {"start": v(-138.15, 254.23) * mm, "end": v(-139.24, 260.66) * mm});
            skLineSegment(sketch, "E408", {"start": v(-139.24, 260.66) * mm, "end": v(-150.82, 398.1) * mm});
            skLineSegment(sketch, "E409", {"start": v(-150.82, 398.1) * mm, "end": v(-150.91, 399.93) * mm});
            skLineSegment(sketch, "E410", {"start": v(-150.91, 399.93) * mm, "end": v(-150.88, 401.73) * mm});
            skLineSegment(sketch, "E411", {"start": v(-150.88, 401.73) * mm, "end": v(-150.73, 403.51) * mm});
            skLineSegment(sketch, "E412", {"start": v(-150.73, 403.51) * mm, "end": v(-150.46, 405.26) * mm});
            skLineSegment(sketch, "E413", {"start": v(-150.46, 405.26) * mm, "end": v(-150.09, 406.97) * mm});
            skLineSegment(sketch, "E414", {"start": v(-150.09, 406.97) * mm, "end": v(-149.6, 408.64) * mm});
            skLineSegment(sketch, "E415", {"start": v(-149.6, 408.64) * mm, "end": v(-149.01, 410.28) * mm});
            skLineSegment(sketch, "E416", {"start": v(-149.01, 410.28) * mm, "end": v(-148.34, 411.83) * mm});
            skLineSegment(sketch, "E417", {"start": v(-148.34, 411.83) * mm, "end": v(-199.48, 411.82) * mm});
            skLineSegment(sketch, "E418", {"start": v(-199.48, 411.82) * mm, "end": v(-199.69, 411.82) * mm});
            skLineSegment(sketch, "E419", {"start": v(-199.69, 411.82) * mm, "end": v(-199.89, 411.78) * mm});
            skLineSegment(sketch, "E420", {"start": v(-199.89, 411.78) * mm, "end": v(-200.07, 411.68) * mm});
            skLineSegment(sketch, "E421", {"start": v(-200.07, 411.68) * mm, "end": v(-200.24, 411.54) * mm});
            skLineSegment(sketch, "E422", {"start": v(-200.24, 411.54) * mm, "end": v(-200.37, 411.38) * mm});
            skLineSegment(sketch, "E423", {"start": v(-200.37, 411.38) * mm, "end": v(-200.48, 411.2) * mm});
            skLineSegment(sketch, "E424", {"start": v(-200.48, 411.2) * mm, "end": v(-200.54, 411) * mm});
            skLineSegment(sketch, "E425", {"start": v(-200.54, 411) * mm, "end": v(-200.56, 410.78) * mm});
            skLineSegment(sketch, "E426", {"start": v(-200.56, 410.78) * mm, "end": v(-200.57, 382.2) * mm});
            skLineSegment(sketch, "E427", {"start": v(-200.57, 382.2) * mm, "end": v(-200.57, 352.67) * mm});
            skLineSegment(sketch, "E428", {"start": v(-200.57, 352.67) * mm, "end": v(-200.58, 322.52) * mm});
            skLineSegment(sketch, "E429", {"start": v(-200.58, 322.52) * mm, "end": v(-200.6, 292.05) * mm});
            skLineSegment(sketch, "E430", {"start": v(-200.6, 292.05) * mm, "end": v(-200.6, 261.6) * mm});
            skLineSegment(sketch, "E431", {"start": v(-200.6, 261.6) * mm, "end": v(-200.6, 231.44) * mm});
            skLineSegment(sketch, "E432", {"start": v(-200.6, 231.44) * mm, "end": v(-200.6, 201.92) * mm});
            skLineSegment(sketch, "E433", {"start": v(-200.6, 201.92) * mm, "end": v(-200.58, 173.33) * mm});
            skLineSegment(sketch, "E434", {"start": v(-200.58, 173.33) * mm, "end": v(-200.37, 167.7) * mm});
            skLineSegment(sketch, "E435", {"start": v(-200.37, 167.7) * mm, "end": v(-199.65, 162.78) * mm});
            skLineSegment(sketch, "E436", {"start": v(-199.65, 162.78) * mm, "end": v(-198.42, 158.56) * mm});
            skLineSegment(sketch, "E437", {"start": v(-198.42, 158.56) * mm, "end": v(-196.67, 155.06) * mm});
            skLineSegment(sketch, "E438", {"start": v(-196.67, 155.06) * mm, "end": v(-194.4, 152.28) * mm});
            skLineSegment(sketch, "E439", {"start": v(-194.4, 152.28) * mm, "end": v(-191.58, 150.23) * mm});
            skLineSegment(sketch, "E440", {"start": v(-191.58, 150.23) * mm, "end": v(-188.23, 148.93) * mm});
            skLineSegment(sketch, "E441", {"start": v(-188.23, 148.93) * mm, "end": v(-184.34, 148.38) * mm});
            skLineSegment(sketch, "E442", {"start": v(-184.34, 148.38) * mm, "end": v(-155.1, 148.43) * mm});
            skLineSegment(sketch, "E443", {"start": v(-155.1, 148.43) * mm, "end": v(-145.74, 148.43) * mm});
            skLineSegment(sketch, "E444", {"start": v(-145.74, 148.43) * mm, "end": v(-142.4, 148.13) * mm});
            skLineSegment(sketch, "E445", {"start": v(-142.4, 148.13) * mm, "end": v(-139.46, 147.2) * mm});
            skLineSegment(sketch, "E446", {"start": v(-139.46, 147.2) * mm, "end": v(-136.94, 145.71) * mm});
            skLineSegment(sketch, "E447", {"start": v(-136.94, 145.71) * mm, "end": v(-134.85, 143.73) * mm});
            skLineSegment(sketch, "E448", {"start": v(-134.85, 143.73) * mm, "end": v(-133.2, 141.32) * mm});
            skLineSegment(sketch, "E449", {"start": v(-133.2, 141.32) * mm, "end": v(-131.98, 138.56) * mm});
            skLineSegment(sketch, "E450", {"start": v(-131.98, 138.56) * mm, "end": v(-131.22, 135.53) * mm});
            skLineSegment(sketch, "E451", {"start": v(-131.22, 135.53) * mm, "end": v(-130.91, 132.28) * mm});
            skLineSegment(sketch, "E452", {"start": v(-130.91, 132.28) * mm, "end": v(-130.9, 132.18) * mm});
            skLineSegment(sketch, "E453", {"start": v(-130.9, 132.18) * mm, "end": v(-130.9, 116.76) * mm});
            skLineSegment(sketch, "E454", {"start": v(-130.9, 116.76) * mm, "end": v(-130.92, 116.55) * mm});
            skLineSegment(sketch, "E455", {"start": v(-130.92, 116.55) * mm, "end": v(-131.05, 114.52) * mm});
            skLineSegment(sketch, "E456", {"start": v(-131.05, 114.52) * mm, "end": v(-131.28, 112.51) * mm});
            skLineSegment(sketch, "E457", {"start": v(-131.28, 112.51) * mm, "end": v(-131.6, 110.52) * mm});
            skLineSegment(sketch, "E458", {"start": v(-131.6, 110.52) * mm, "end": v(-132, 108.56) * mm});
            skLineSegment(sketch, "E459", {"start": v(-132, 108.56) * mm, "end": v(-132.52, 106.61) * mm});
            skLineSegment(sketch, "E460", {"start": v(-132.52, 106.61) * mm, "end": v(-133.14, 104.7) * mm});
            skLineSegment(sketch, "E461", {"start": v(-133.14, 104.7) * mm, "end": v(-133.85, 102.8) * mm});
            skLineSegment(sketch, "E462", {"start": v(-133.85, 102.8) * mm, "end": v(-134.68, 100.95) * mm});
            skLineSegment(sketch, "E463", {"start": v(-134.68, 100.95) * mm, "end": v(-134.82, 100.66) * mm});
            skLineSegment(sketch, "E464", {"start": v(-134.82, 100.66) * mm, "end": v(-224.4, -13.84) * mm});
            skLineSegment(sketch, "E465", {"start": v(-224.4, -13.84) * mm, "end": v(-224.88, -14.96) * mm});
            skLineSegment(sketch, "E466", {"start": v(-224.88, -14.96) * mm, "end": v(-225.28, -16.13) * mm});
            skLineSegment(sketch, "E467", {"start": v(-225.28, -16.13) * mm, "end": v(-225.6, -17.34) * mm});
            skLineSegment(sketch, "E468", {"start": v(-225.6, -17.34) * mm, "end": v(-225.84, -18.58) * mm});
            skLineSegment(sketch, "E469", {"start": v(-225.84, -18.58) * mm, "end": v(-226.02, -19.82) * mm});
            skLineSegment(sketch, "E470", {"start": v(-226.02, -19.82) * mm, "end": v(-226.15, -21.07) * mm});
            skLineSegment(sketch, "E471", {"start": v(-226.15, -21.07) * mm, "end": v(-226.22, -22.3) * mm});
            skLineSegment(sketch, "E472", {"start": v(-226.22, -22.3) * mm, "end": v(-226.26, -23.51) * mm});
            skLineSegment(sketch, "E473", {"start": v(-226.26, -23.51) * mm, "end": v(-226.26, -219.17) * mm});
            skLineSegment(sketch, "E474", {"start": v(-226.26, -219.17) * mm, "end": v(-225.04, -231.16) * mm});
            skLineSegment(sketch, "E475", {"start": v(-225.04, -231.16) * mm, "end": v(-221.55, -242.34) * mm});
            skLineSegment(sketch, "E476", {"start": v(-221.55, -242.34) * mm, "end": v(-216.02, -252.48) * mm});
            skLineSegment(sketch, "E477", {"start": v(-216.02, -252.48) * mm, "end": v(-208.71, -261.33) * mm});
            skLineSegment(sketch, "E478", {"start": v(-208.71, -261.33) * mm, "end": v(-199.87, -268.64) * mm});
            skLineSegment(sketch, "E479", {"start": v(-199.87, -268.64) * mm, "end": v(-189.73, -274.16) * mm});
            skLineSegment(sketch, "E480", {"start": v(-189.73, -274.16) * mm, "end": v(-178.54, -277.65) * mm});
            skLineSegment(sketch, "E481", {"start": v(-178.54, -277.65) * mm, "end": v(-166.56, -278.87) * mm});
            skLineSegment(sketch, "E482", {"start": v(-166.56, -278.87) * mm, "end": v(163.52, -279.98) * mm});
            skLineSegment(sketch, "E483", {"start": v(163.52, -279.98) * mm, "end": v(175.51, -278.76) * mm});
            skLineSegment(sketch, "E484", {"start": v(175.51, -278.76) * mm, "end": v(186.7, -275.27) * mm});
            skLineSegment(sketch, "E485", {"start": v(186.7, -275.27) * mm, "end": v(196.84, -269.75) * mm});
            skLineSegment(sketch, "E486", {"start": v(196.84, -269.75) * mm, "end": v(205.68, -262.44) * mm});
            skLineSegment(sketch, "E487", {"start": v(205.68, -262.44) * mm, "end": v(213, -253.6) * mm});
            skLineSegment(sketch, "E488", {"start": v(213, -253.6) * mm, "end": v(218.51, -243.45) * mm});
            skLineSegment(sketch, "E489", {"start": v(218.51, -243.45) * mm, "end": v(222, -232.27) * mm});
            skLineSegment(sketch, "E490", {"start": v(222, -232.27) * mm, "end": v(223.23, -220.28) * mm});
            skLineSegment(sketch, "E491", {"start": v(223.23, -220.28) * mm, "end": v(223.22, -24.14) * mm});
            skLineSegment(sketch, "E492", {"start": v(-206.85, 480.96) * mm, "end": v(204.04, 480.96) * mm});
            skLineSegment(sketch, "E493", {"start": v(204.04, 480.96) * mm, "end": v(204.04, 411.87) * mm});
            skLineSegment(sketch, "E494", {"start": v(204.04, 411.87) * mm, "end": v(145.2, 411.87) * mm});
            skLineSegment(sketch, "E495", {"start": v(145.2, 411.87) * mm, "end": v(143, 415.76) * mm});
            skLineSegment(sketch, "E496", {"start": v(143, 415.76) * mm, "end": v(140.23, 419.3) * mm});
            skLineSegment(sketch, "E497", {"start": v(140.23, 419.3) * mm, "end": v(136.97, 422.42) * mm});
            skLineSegment(sketch, "E498", {"start": v(136.97, 422.42) * mm, "end": v(133.27, 425.1) * mm});
            skLineSegment(sketch, "E499", {"start": v(133.27, 425.1) * mm, "end": v(129.21, 427.26) * mm});
            skLineSegment(sketch, "E500", {"start": v(129.21, 427.26) * mm, "end": v(124.87, 428.87) * mm});
            skLineSegment(sketch, "E501", {"start": v(124.87, 428.87) * mm, "end": v(120.3, 429.87) * mm});
            skLineSegment(sketch, "E502", {"start": v(120.3, 429.87) * mm, "end": v(115.58, 430.21) * mm});
            skLineSegment(sketch, "E503", {"start": v(115.58, 430.21) * mm, "end": v(-118.7, 430.21) * mm});
            skLineSegment(sketch, "E504", {"start": v(-118.7, 430.21) * mm, "end": v(-123.42, 429.87) * mm});
            skLineSegment(sketch, "E505", {"start": v(-123.42, 429.87) * mm, "end": v(-127.99, 428.87) * mm});
            skLineSegment(sketch, "E506", {"start": v(-127.99, 428.87) * mm, "end": v(-132.34, 427.26) * mm});
            skLineSegment(sketch, "E507", {"start": v(-132.34, 427.26) * mm, "end": v(-136.4, 425.1) * mm});
            skLineSegment(sketch, "E508", {"start": v(-136.4, 425.1) * mm, "end": v(-140.09, 422.42) * mm});
            skLineSegment(sketch, "E509", {"start": v(-140.09, 422.42) * mm, "end": v(-143.35, 419.3) * mm});
            skLineSegment(sketch, "E510", {"start": v(-143.35, 419.3) * mm, "end": v(-146.12, 415.76) * mm});
            skLineSegment(sketch, "E511", {"start": v(-146.12, 415.76) * mm, "end": v(-148.33, 411.87) * mm});
            skLineSegment(sketch, "E512", {"start": v(-148.33, 411.87) * mm, "end": v(-206.85, 411.87) * mm});
            skLineSegment(sketch, "E513", {"start": v(-206.85, 411.87) * mm, "end": v(-206.85, 480.96) * mm});
            skLineSegment(sketch, "E514", {"start": v(206.56, -273.9) * mm, "end": v(206.69, -315) * mm});
            skLineSegment(sketch, "E515", {"start": v(206.69, -315) * mm, "end": v(203.69, -315.98) * mm});
            skLineSegment(sketch, "E516", {"start": v(203.69, -315.98) * mm, "end": v(200.63, -316.82) * mm});
            skLineSegment(sketch, "E517", {"start": v(200.63, -316.82) * mm, "end": v(197.52, -317.52) * mm});
            skLineSegment(sketch, "E518", {"start": v(197.52, -317.52) * mm, "end": v(194.37, -318.08) * mm});
            skLineSegment(sketch, "E519", {"start": v(194.37, -318.08) * mm, "end": v(191.17, -318.5) * mm});
            skLineSegment(sketch, "E520", {"start": v(191.17, -318.5) * mm, "end": v(187.93, -318.8) * mm});
            skLineSegment(sketch, "E521", {"start": v(187.93, -318.8) * mm, "end": v(184.65, -318.98) * mm});
            skLineSegment(sketch, "E522", {"start": v(184.65, -318.98) * mm, "end": v(181.35, -319.04) * mm});
            skLineSegment(sketch, "E523", {"start": v(181.35, -319.04) * mm, "end": v(-184.36, -319.04) * mm});
            skLineSegment(sketch, "E524", {"start": v(-184.36, -319.04) * mm, "end": v(-187.66, -318.98) * mm});
            skLineSegment(sketch, "E525", {"start": v(-187.66, -318.98) * mm, "end": v(-190.93, -318.8) * mm});
            skLineSegment(sketch, "E526", {"start": v(-190.93, -318.8) * mm, "end": v(-194.15, -318.5) * mm});
            skLineSegment(sketch, "E527", {"start": v(-194.15, -318.5) * mm, "end": v(-197.34, -318.07) * mm});
            skLineSegment(sketch, "E528", {"start": v(-197.34, -318.07) * mm, "end": v(-200.48, -317.51) * mm});
            skLineSegment(sketch, "E529", {"start": v(-200.48, -317.51) * mm, "end": v(-203.58, -316.82) * mm});
            skLineSegment(sketch, "E530", {"start": v(-203.58, -316.82) * mm, "end": v(-206.62, -315.98) * mm});
            skLineSegment(sketch, "E531", {"start": v(-206.62, -315.98) * mm, "end": v(-209.62, -315) * mm});
            skLineSegment(sketch, "E532", {"start": v(-209.62, -315) * mm, "end": v(-209.49, -273.9) * mm});
            skLineSegment(sketch, "E533", {"start": v(-209.49, -273.9) * mm, "end": v(-201.87, -278.94) * mm});
            skLineSegment(sketch, "E534", {"start": v(-201.87, -278.94) * mm, "end": v(-194.9, -282.67) * mm});
            skLineSegment(sketch, "E535", {"start": v(-194.9, -282.67) * mm, "end": v(-188.09, -285.3) * mm});
            skLineSegment(sketch, "E536", {"start": v(-188.09, -285.3) * mm, "end": v(-181, -287.01) * mm});
            skLineSegment(sketch, "E537", {"start": v(-181, -287.01) * mm, "end": v(-173.2, -288) * mm});
            skLineSegment(sketch, "E538", {"start": v(-173.2, -288) * mm, "end": v(-164.2, -288.47) * mm});
            skLineSegment(sketch, "E539", {"start": v(-164.2, -288.47) * mm, "end": v(-153.56, -288.61) * mm});
            skLineSegment(sketch, "E540", {"start": v(-153.56, -288.61) * mm, "end": v(-140.82, -288.61) * mm});
            skLineSegment(sketch, "E541", {"start": v(-140.82, -288.61) * mm, "end": v(137.8, -288.61) * mm});
            skLineSegment(sketch, "E542", {"start": v(137.8, -288.61) * mm, "end": v(155.52, -288.58) * mm});
            skLineSegment(sketch, "E543", {"start": v(155.52, -288.58) * mm, "end": v(163.1, -288.55) * mm});
            skLineSegment(sketch, "E544", {"start": v(163.1, -288.55) * mm, "end": v(170.34, -288.03) * mm});
            skLineSegment(sketch, "E545", {"start": v(170.34, -288.03) * mm, "end": v(177.25, -287.01) * mm});
            skLineSegment(sketch, "E546", {"start": v(177.25, -287.01) * mm, "end": v(183.83, -285.47) * mm});
            skLineSegment(sketch, "E547", {"start": v(183.83, -285.47) * mm, "end": v(190.05, -283.4) * mm});
            skLineSegment(sketch, "E548", {"start": v(190.05, -283.4) * mm, "end": v(195.92, -280.8) * mm});
            skLineSegment(sketch, "E549", {"start": v(195.92, -280.8) * mm, "end": v(201.43, -277.63) * mm});
            skLineSegment(sketch, "E550", {"start": v(201.43, -277.63) * mm, "end": v(206.56, -273.9) * mm});
            skLineSegment(sketch, "E551", {"start": v(161.49, -23.19) * mm, "end": v(167.4, -27.32) * mm});
            skLineSegment(sketch, "E552", {"start": v(167.4, -27.32) * mm, "end": v(172.14, -32.08) * mm});
            skLineSegment(sketch, "E553", {"start": v(172.14, -32.08) * mm, "end": v(175.85, -37.39) * mm});
            skLineSegment(sketch, "E554", {"start": v(175.85, -37.39) * mm, "end": v(178.64, -43.17) * mm});
            skLineSegment(sketch, "E555", {"start": v(178.64, -43.17) * mm, "end": v(180.6, -49.35) * mm});
            skLineSegment(sketch, "E556", {"start": v(180.6, -49.35) * mm, "end": v(181.88, -55.85) * mm});
            skLineSegment(sketch, "E557", {"start": v(181.88, -55.85) * mm, "end": v(182.55, -62.6) * mm});
            skLineSegment(sketch, "E558", {"start": v(182.55, -62.6) * mm, "end": v(182.75, -69.5) * mm});
            skLineSegment(sketch, "E559", {"start": v(182.75, -69.5) * mm, "end": v(182.75, -215.7) * mm});
            skLineSegment(sketch, "E560", {"start": v(182.75, -215.7) * mm, "end": v(182.7, -216.23) * mm});
            skLineSegment(sketch, "E561", {"start": v(182.7, -216.23) * mm, "end": v(181.83, -221.53) * mm});
            skLineSegment(sketch, "E562", {"start": v(181.83, -221.53) * mm, "end": v(180.44, -226.56) * mm});
            skLineSegment(sketch, "E563", {"start": v(180.44, -226.56) * mm, "end": v(178.51, -231.3) * mm});
            skLineSegment(sketch, "E564", {"start": v(178.51, -231.3) * mm, "end": v(176.07, -235.71) * mm});
            skLineSegment(sketch, "E565", {"start": v(176.07, -235.71) * mm, "end": v(173.1, -239.8) * mm});
            skLineSegment(sketch, "E566", {"start": v(173.1, -239.8) * mm, "end": v(169.65, -243.55) * mm});
            skLineSegment(sketch, "E567", {"start": v(169.65, -243.55) * mm, "end": v(165.68, -246.92) * mm});
            skLineSegment(sketch, "E568", {"start": v(165.68, -246.92) * mm, "end": v(161.22, -249.9) * mm});
            skLineSegment(sketch, "E569", {"start": v(161.22, -249.9) * mm, "end": v(158.7, -251.28) * mm});
            skLineSegment(sketch, "E570", {"start": v(158.7, -251.28) * mm, "end": v(155.92, -252.59) * mm});
            skLineSegment(sketch, "E571", {"start": v(155.92, -252.59) * mm, "end": v(152.98, -253.79) * mm});
            skLineSegment(sketch, "E572", {"start": v(152.98, -253.79) * mm, "end": v(149.92, -254.84) * mm});
            skLineSegment(sketch, "E573", {"start": v(149.92, -254.84) * mm, "end": v(146.8, -255.73) * mm});
            skLineSegment(sketch, "E574", {"start": v(146.8, -255.73) * mm, "end": v(143.7, -256.4) * mm});
            skLineSegment(sketch, "E575", {"start": v(143.7, -256.4) * mm, "end": v(140.66, -256.82) * mm});
            skLineSegment(sketch, "E576", {"start": v(140.66, -256.82) * mm, "end": v(137.75, -256.97) * mm});
            skLineSegment(sketch, "E577", {"start": v(137.75, -256.97) * mm, "end": v(-140.86, -256.97) * mm});
            skLineSegment(sketch, "E578", {"start": v(-140.86, -256.97) * mm, "end": v(-143.77, -256.82) * mm});
            skLineSegment(sketch, "E579", {"start": v(-143.77, -256.82) * mm, "end": v(-146.8, -256.4) * mm});
            skLineSegment(sketch, "E580", {"start": v(-146.8, -256.4) * mm, "end": v(-149.91, -255.73) * mm});
            skLineSegment(sketch, "E581", {"start": v(-149.91, -255.73) * mm, "end": v(-153.03, -254.84) * mm});
            skLineSegment(sketch, "E582", {"start": v(-153.03, -254.84) * mm, "end": v(-156.09, -253.79) * mm});
            skLineSegment(sketch, "E583", {"start": v(-156.09, -253.79) * mm, "end": v(-159.03, -252.59) * mm});
            skLineSegment(sketch, "E584", {"start": v(-159.03, -252.59) * mm, "end": v(-161.8, -251.28) * mm});
            skLineSegment(sketch, "E585", {"start": v(-161.8, -251.28) * mm, "end": v(-164.33, -249.9) * mm});
            skLineSegment(sketch, "E586", {"start": v(-164.33, -249.9) * mm, "end": v(-168.8, -246.92) * mm});
            skLineSegment(sketch, "E587", {"start": v(-168.8, -246.92) * mm, "end": v(-172.76, -243.55) * mm});
            skLineSegment(sketch, "E588", {"start": v(-172.76, -243.55) * mm, "end": v(-176.22, -239.8) * mm});
            skLineSegment(sketch, "E589", {"start": v(-176.22, -239.8) * mm, "end": v(-179.18, -235.71) * mm});
            skLineSegment(sketch, "E590", {"start": v(-179.18, -235.71) * mm, "end": v(-181.62, -231.3) * mm});
            skLineSegment(sketch, "E591", {"start": v(-181.62, -231.3) * mm, "end": v(-183.55, -226.56) * mm});
            skLineSegment(sketch, "E592", {"start": v(-183.55, -226.56) * mm, "end": v(-184.94, -221.53) * mm});
            skLineSegment(sketch, "E593", {"start": v(-184.94, -221.53) * mm, "end": v(-185.8, -216.23) * mm});
            skLineSegment(sketch, "E594", {"start": v(-185.8, -216.23) * mm, "end": v(-185.86, -215.7) * mm});
            skLineSegment(sketch, "E595", {"start": v(-185.86, -215.7) * mm, "end": v(-185.86, -69.5) * mm});
            skLineSegment(sketch, "E596", {"start": v(-185.86, -69.5) * mm, "end": v(-185.66, -62.6) * mm});
            skLineSegment(sketch, "E597", {"start": v(-185.66, -62.6) * mm, "end": v(-184.99, -55.85) * mm});
            skLineSegment(sketch, "E598", {"start": v(-184.99, -55.85) * mm, "end": v(-183.72, -49.35) * mm});
            skLineSegment(sketch, "E599", {"start": v(-183.72, -49.35) * mm, "end": v(-181.75, -43.17) * mm});
            skLineSegment(sketch, "E600", {"start": v(-181.75, -43.17) * mm, "end": v(-178.97, -37.39) * mm});
            skLineSegment(sketch, "E601", {"start": v(-178.97, -37.39) * mm, "end": v(-175.25, -32.08) * mm});
            skLineSegment(sketch, "E602", {"start": v(-175.25, -32.08) * mm, "end": v(-170.5, -27.32) * mm});
            skLineSegment(sketch, "E603", {"start": v(-170.5, -27.32) * mm, "end": v(-164.6, -23.19) * mm});
            skLineSegment(sketch, "E604", {"start": v(-164.6, -23.19) * mm, "end": v(-162.28, -21.74) * mm});
            skLineSegment(sketch, "E605", {"start": v(-162.28, -21.74) * mm, "end": v(-159.96, -20.31) * mm});
            skLineSegment(sketch, "E606", {"start": v(-159.96, -20.31) * mm, "end": v(-157.63, -18.9) * mm});
            skLineSegment(sketch, "E607", {"start": v(-157.63, -18.9) * mm, "end": v(-155.3, -17.48) * mm});
            skLineSegment(sketch, "E608", {"start": v(-155.3, -17.48) * mm, "end": v(-152.97, -16.06) * mm});
            skLineSegment(sketch, "E609", {"start": v(-152.97, -16.06) * mm, "end": v(-150.64, -14.64) * mm});
            skLineSegment(sketch, "E610", {"start": v(-150.64, -14.64) * mm, "end": v(-148.31, -13.21) * mm});
            skLineSegment(sketch, "E611", {"start": v(-148.31, -13.21) * mm, "end": v(-146, -11.77) * mm});
            skLineSegment(sketch, "E612", {"start": v(-146, -11.77) * mm, "end": v(-144.58, -10.89) * mm});
            skLineSegment(sketch, "E613", {"start": v(-144.58, -10.89) * mm, "end": v(-143.17, -10) * mm});
            skLineSegment(sketch, "E614", {"start": v(-143.17, -10) * mm, "end": v(-141.76, -9.1) * mm});
            skLineSegment(sketch, "E615", {"start": v(-141.76, -9.1) * mm, "end": v(-140.35, -8.18) * mm});
            skLineSegment(sketch, "E616", {"start": v(-140.35, -8.18) * mm, "end": v(-138.95, -7.27) * mm});
            skLineSegment(sketch, "E617", {"start": v(-138.95, -7.27) * mm, "end": v(-137.55, -6.34) * mm});
            skLineSegment(sketch, "E618", {"start": v(-137.55, -6.34) * mm, "end": v(-136.16, -5.4) * mm});
            skLineSegment(sketch, "E619", {"start": v(-136.16, -5.4) * mm, "end": v(-134.79, -4.46) * mm});
            skLineSegment(sketch, "E620", {"start": v(-134.79, -4.46) * mm, "end": v(-134.22, -4.06) * mm});
            skLineSegment(sketch, "E621", {"start": v(-134.22, -4.06) * mm, "end": v(-133.57, -3.61) * mm});
            skLineSegment(sketch, "E622", {"start": v(-133.57, -3.61) * mm, "end": v(-132.88, -3.12) * mm});
            skLineSegment(sketch, "E623", {"start": v(-132.88, -3.12) * mm, "end": v(-132.16, -2.6) * mm});
            skLineSegment(sketch, "E624", {"start": v(-132.16, -2.6) * mm, "end": v(-131.43, -2.07) * mm});
            skLineSegment(sketch, "E625", {"start": v(-131.43, -2.07) * mm, "end": v(-130.74, -1.53) * mm});
            skLineSegment(sketch, "E626", {"start": v(-130.74, -1.53) * mm, "end": v(-130.1, -1) * mm});
            skLineSegment(sketch, "E627", {"start": v(-130.1, -1) * mm, "end": v(-129.52, -0.48) * mm});
            skLineSegment(sketch, "E628", {"start": v(-129.52, -0.48) * mm, "end": v(-95.38, 79.7) * mm});
            skLineSegment(sketch, "E629", {"start": v(-95.38, 79.7) * mm, "end": v(-93.88, 83.87) * mm});
            skLineSegment(sketch, "E630", {"start": v(-93.88, 83.87) * mm, "end": v(-92.83, 88.17) * mm});
            skLineSegment(sketch, "E631", {"start": v(-92.83, 88.17) * mm, "end": v(-92.13, 92.56) * mm});
            skLineSegment(sketch, "E632", {"start": v(-92.13, 92.56) * mm, "end": v(-91.7, 97.01) * mm});
            skLineSegment(sketch, "E633", {"start": v(-91.7, 97.01) * mm, "end": v(-91.48, 101.5) * mm});
            skLineSegment(sketch, "E634", {"start": v(-91.48, 101.5) * mm, "end": v(-91.37, 105.99) * mm});
            skLineSegment(sketch, "E635", {"start": v(-91.37, 105.99) * mm, "end": v(-91.29, 110.44) * mm});
            skLineSegment(sketch, "E636", {"start": v(-91.29, 110.44) * mm, "end": v(-91.15, 114.84) * mm});
            skLineSegment(sketch, "E637", {"start": v(-91.15, 114.84) * mm, "end": v(-91.1, 115.9) * mm});
            skLineSegment(sketch, "E638", {"start": v(-91.1, 115.9) * mm, "end": v(-91.1, 132.58) * mm});
            skLineSegment(sketch, "E639", {"start": v(-91.1, 132.58) * mm, "end": v(-91.13, 143.67) * mm});
            skLineSegment(sketch, "E640", {"start": v(-91.13, 143.67) * mm, "end": v(-91.13, 144.19) * mm});
            skLineSegment(sketch, "E641", {"start": v(-91.13, 144.19) * mm, "end": v(-91.12, 144.7) * mm});
            skLineSegment(sketch, "E642", {"start": v(-91.12, 144.7) * mm, "end": v(-91.1, 145.23) * mm});
            skLineSegment(sketch, "E643", {"start": v(-91.1, 145.23) * mm, "end": v(-91.08, 145.76) * mm});
            skLineSegment(sketch, "E644", {"start": v(-91.08, 145.76) * mm, "end": v(-91.05, 146.28) * mm});
            skLineSegment(sketch, "E645", {"start": v(-91.05, 146.28) * mm, "end": v(-91.01, 146.8) * mm});
            skLineSegment(sketch, "E646", {"start": v(-91.01, 146.8) * mm, "end": v(-90.96, 147.33) * mm});
            skLineSegment(sketch, "E647", {"start": v(-90.96, 147.33) * mm, "end": v(-90.9, 147.84) * mm});
            skLineSegment(sketch, "E648", {"start": v(-90.9, 147.84) * mm, "end": v(-89.83, 155.61) * mm});
            skLineSegment(sketch, "E649", {"start": v(-89.83, 155.61) * mm, "end": v(-82.03, 156.4) * mm});
            skLineSegment(sketch, "E650", {"start": v(-82.03, 156.4) * mm, "end": v(-81.43, 156.45) * mm});
            skLineSegment(sketch, "E651", {"start": v(-81.43, 156.45) * mm, "end": v(-80.82, 156.48) * mm});
            skLineSegment(sketch, "E652", {"start": v(-80.82, 156.48) * mm, "end": v(-80.21, 156.5) * mm});
            skLineSegment(sketch, "E653", {"start": v(-80.21, 156.5) * mm, "end": v(-79.6, 156.51) * mm});
            skLineSegment(sketch, "E654", {"start": v(-79.6, 156.51) * mm, "end": v(76.5, 156.51) * mm});
            skLineSegment(sketch, "E655", {"start": v(76.5, 156.51) * mm, "end": v(77.1, 156.5) * mm});
            skLineSegment(sketch, "E656", {"start": v(77.1, 156.5) * mm, "end": v(77.7, 156.48) * mm});
            skLineSegment(sketch, "E657", {"start": v(77.7, 156.48) * mm, "end": v(78.32, 156.45) * mm});
            skLineSegment(sketch, "E658", {"start": v(78.32, 156.45) * mm, "end": v(78.92, 156.4) * mm});
            skLineSegment(sketch, "E659", {"start": v(78.92, 156.4) * mm, "end": v(86.72, 155.61) * mm});
            skLineSegment(sketch, "E660", {"start": v(86.72, 155.61) * mm, "end": v(87.78, 147.84) * mm});
            skLineSegment(sketch, "E661", {"start": v(87.78, 147.84) * mm, "end": v(87.85, 147.33) * mm});
            skLineSegment(sketch, "E662", {"start": v(87.85, 147.33) * mm, "end": v(87.9, 146.8) * mm});
            skLineSegment(sketch, "E663", {"start": v(87.9, 146.8) * mm, "end": v(87.94, 146.28) * mm});
            skLineSegment(sketch, "E664", {"start": v(87.94, 146.28) * mm, "end": v(87.97, 145.76) * mm});
            skLineSegment(sketch, "E665", {"start": v(87.97, 145.76) * mm, "end": v(88, 145.23) * mm});
            skLineSegment(sketch, "E666", {"start": v(88, 145.23) * mm, "end": v(88, 144.7) * mm});
            skLineSegment(sketch, "E667", {"start": v(88, 144.7) * mm, "end": v(88.02, 144.19) * mm});
            skLineSegment(sketch, "E668", {"start": v(88.02, 144.19) * mm, "end": v(88.02, 143.67) * mm});
            skLineSegment(sketch, "E669", {"start": v(88.02, 143.67) * mm, "end": v(88, 132.6) * mm});
            skLineSegment(sketch, "E670", {"start": v(88, 132.6) * mm, "end": v(88, 115.9) * mm});
            skLineSegment(sketch, "E671", {"start": v(88, 115.9) * mm, "end": v(88.04, 114.84) * mm});
            skLineSegment(sketch, "E672", {"start": v(88.04, 114.84) * mm, "end": v(88.18, 110.44) * mm});
            skLineSegment(sketch, "E673", {"start": v(88.18, 110.44) * mm, "end": v(88.26, 105.99) * mm});
            skLineSegment(sketch, "E674", {"start": v(88.26, 105.99) * mm, "end": v(88.37, 101.5) * mm});
            skLineSegment(sketch, "E675", {"start": v(88.37, 101.5) * mm, "end": v(88.6, 97.01) * mm});
            skLineSegment(sketch, "E676", {"start": v(88.6, 97.01) * mm, "end": v(89.02, 92.56) * mm});
            skLineSegment(sketch, "E677", {"start": v(89.02, 92.56) * mm, "end": v(89.72, 88.17) * mm});
            skLineSegment(sketch, "E678", {"start": v(89.72, 88.17) * mm, "end": v(90.77, 83.87) * mm});
            skLineSegment(sketch, "E679", {"start": v(90.77, 83.87) * mm, "end": v(92.27, 79.7) * mm});
            skLineSegment(sketch, "E680", {"start": v(92.27, 79.7) * mm, "end": v(126.4, -0.48) * mm});
            skLineSegment(sketch, "E681", {"start": v(126.4, -0.48) * mm, "end": v(126.98, -1) * mm});
            skLineSegment(sketch, "E682", {"start": v(126.98, -1) * mm, "end": v(127.63, -1.53) * mm});
            skLineSegment(sketch, "E683", {"start": v(127.63, -1.53) * mm, "end": v(128.32, -2.07) * mm});
            skLineSegment(sketch, "E684", {"start": v(128.32, -2.07) * mm, "end": v(129.05, -2.6) * mm});
            skLineSegment(sketch, "E685", {"start": v(129.05, -2.6) * mm, "end": v(129.77, -3.12) * mm});
            skLineSegment(sketch, "E686", {"start": v(129.77, -3.12) * mm, "end": v(130.46, -3.61) * mm});
            skLineSegment(sketch, "E687", {"start": v(130.46, -3.61) * mm, "end": v(131.1, -4.06) * mm});
            skLineSegment(sketch, "E688", {"start": v(131.1, -4.06) * mm, "end": v(131.68, -4.46) * mm});
            skLineSegment(sketch, "E689", {"start": v(131.68, -4.46) * mm, "end": v(133.05, -5.4) * mm});
            skLineSegment(sketch, "E690", {"start": v(133.05, -5.4) * mm, "end": v(134.44, -6.34) * mm});
            skLineSegment(sketch, "E691", {"start": v(134.44, -6.34) * mm, "end": v(135.84, -7.27) * mm});
            skLineSegment(sketch, "E692", {"start": v(135.84, -7.27) * mm, "end": v(137.24, -8.18) * mm});
            skLineSegment(sketch, "E693", {"start": v(137.24, -8.18) * mm, "end": v(138.64, -9.1) * mm});
            skLineSegment(sketch, "E694", {"start": v(138.64, -9.1) * mm, "end": v(140.06, -10) * mm});
            skLineSegment(sketch, "E695", {"start": v(140.06, -10) * mm, "end": v(141.47, -10.89) * mm});
            skLineSegment(sketch, "E696", {"start": v(141.47, -10.89) * mm, "end": v(142.89, -11.77) * mm});
            skLineSegment(sketch, "E697", {"start": v(142.89, -11.77) * mm, "end": v(145.2, -13.21) * mm});
            skLineSegment(sketch, "E698", {"start": v(145.2, -13.21) * mm, "end": v(147.53, -14.64) * mm});
            skLineSegment(sketch, "E699", {"start": v(147.53, -14.64) * mm, "end": v(149.86, -16.06) * mm});
            skLineSegment(sketch, "E700", {"start": v(149.86, -16.06) * mm, "end": v(152.2, -17.48) * mm});
            skLineSegment(sketch, "E701", {"start": v(152.2, -17.48) * mm, "end": v(154.52, -18.9) * mm});
            skLineSegment(sketch, "E702", {"start": v(154.52, -18.9) * mm, "end": v(156.85, -20.31) * mm});
            skLineSegment(sketch, "E703", {"start": v(156.85, -20.31) * mm, "end": v(159.17, -21.74) * mm});
            skLineSegment(sketch, "E704", {"start": v(159.17, -21.74) * mm, "end": v(161.49, -23.19) * mm});
            skLineSegment(sketch, "E705", {"start": v(137.75, -247.02) * mm, "end": v(140.67, -246.77) * mm});
            skLineSegment(sketch, "E706", {"start": v(140.67, -246.77) * mm, "end": v(145.07, -245.88) * mm});
            skLineSegment(sketch, "E707", {"start": v(145.07, -245.88) * mm, "end": v(150.4, -244.14) * mm});
            skLineSegment(sketch, "E708", {"start": v(150.4, -244.14) * mm, "end": v(156.17, -241.32) * mm});
            skLineSegment(sketch, "E709", {"start": v(156.17, -241.32) * mm, "end": v(161.81, -237.23) * mm});
            skLineSegment(sketch, "E710", {"start": v(161.81, -237.23) * mm, "end": v(166.82, -231.65) * mm});
            skLineSegment(sketch, "E711", {"start": v(166.82, -231.65) * mm, "end": v(170.66, -224.36) * mm});
            skLineSegment(sketch, "E712", {"start": v(170.66, -224.36) * mm, "end": v(172.8, -215.15) * mm});
            skLineSegment(sketch, "E713", {"start": v(172.8, -215.15) * mm, "end": v(172.8, -69.5) * mm});
            skLineSegment(sketch, "E714", {"start": v(172.8, -69.5) * mm, "end": v(172.76, -65.46) * mm});
            skLineSegment(sketch, "E715", {"start": v(172.76, -65.46) * mm, "end": v(172.5, -60.79) * mm});
            skLineSegment(sketch, "E716", {"start": v(172.5, -60.79) * mm, "end": v(171.86, -55.7) * mm});
            skLineSegment(sketch, "E717", {"start": v(171.86, -55.7) * mm, "end": v(170.64, -50.43) * mm});
            skLineSegment(sketch, "E718", {"start": v(170.64, -50.43) * mm, "end": v(168.66, -45.18) * mm});
            skLineSegment(sketch, "E719", {"start": v(168.66, -45.18) * mm, "end": v(165.74, -40.17) * mm});
            skLineSegment(sketch, "E720", {"start": v(165.74, -40.17) * mm, "end": v(161.7, -35.6) * mm});
            skLineSegment(sketch, "E721", {"start": v(161.7, -35.6) * mm, "end": v(156.34, -31.7) * mm});
            skLineSegment(sketch, "E722", {"start": v(156.34, -31.7) * mm, "end": v(152.28, -29.2) * mm});
            skLineSegment(sketch, "E723", {"start": v(152.28, -29.2) * mm, "end": v(146.93, -25.95) * mm});
            skLineSegment(sketch, "E724", {"start": v(146.93, -25.95) * mm, "end": v(140.83, -22.21) * mm});
            skLineSegment(sketch, "E725", {"start": v(140.83, -22.21) * mm, "end": v(134.51, -18.25) * mm});
            skLineSegment(sketch, "E726", {"start": v(134.51, -18.25) * mm, "end": v(128.5, -14.34) * mm});
            skLineSegment(sketch, "E727", {"start": v(128.5, -14.34) * mm, "end": v(123.36, -10.74) * mm});
            skLineSegment(sketch, "E728", {"start": v(123.36, -10.74) * mm, "end": v(119.58, -7.7) * mm});
            skLineSegment(sketch, "E729", {"start": v(119.58, -7.7) * mm, "end": v(117.73, -5.5) * mm});
            skLineSegment(sketch, "E730", {"start": v(117.73, -5.5) * mm, "end": v(83.12, 75.8) * mm});
            skLineSegment(sketch, "E731", {"start": v(83.12, 75.8) * mm, "end": v(81.34, 80.7) * mm});
            skLineSegment(sketch, "E732", {"start": v(81.34, 80.7) * mm, "end": v(80.07, 85.68) * mm});
            skLineSegment(sketch, "E733", {"start": v(80.07, 85.68) * mm, "end": v(79.23, 90.67) * mm});
            skLineSegment(sketch, "E734", {"start": v(79.23, 90.67) * mm, "end": v(78.72, 95.64) * mm});
            skLineSegment(sketch, "E735", {"start": v(78.72, 95.64) * mm, "end": v(78.45, 100.55) * mm});
            skLineSegment(sketch, "E736", {"start": v(78.45, 100.55) * mm, "end": v(78.32, 105.34) * mm});
            skLineSegment(sketch, "E737", {"start": v(78.32, 105.34) * mm, "end": v(78.23, 109.98) * mm});
            skLineSegment(sketch, "E738", {"start": v(78.23, 109.98) * mm, "end": v(78.1, 114.42) * mm});
            skLineSegment(sketch, "E739", {"start": v(78.1, 114.42) * mm, "end": v(78.05, 115.7) * mm});
            skLineSegment(sketch, "E740", {"start": v(78.05, 115.7) * mm, "end": v(78.05, 132.6) * mm});
            skLineSegment(sketch, "E741", {"start": v(78.05, 132.6) * mm, "end": v(78.07, 143.69) * mm});
            skLineSegment(sketch, "E742", {"start": v(78.07, 143.69) * mm, "end": v(78.06, 144.25) * mm});
            skLineSegment(sketch, "E743", {"start": v(78.06, 144.25) * mm, "end": v(78.05, 144.96) * mm});
            skLineSegment(sketch, "E744", {"start": v(78.05, 144.96) * mm, "end": v(78, 145.74) * mm});
            skLineSegment(sketch, "E745", {"start": v(78, 145.74) * mm, "end": v(77.93, 146.5) * mm});
            skLineSegment(sketch, "E746", {"start": v(77.93, 146.5) * mm, "end": v(76.5, 146.56) * mm});
            skLineSegment(sketch, "E747", {"start": v(76.5, 146.56) * mm, "end": v(-79.6, 146.56) * mm});
            skLineSegment(sketch, "E748", {"start": v(-79.6, 146.56) * mm, "end": v(-81.04, 146.5) * mm});
            skLineSegment(sketch, "E749", {"start": v(-81.04, 146.5) * mm, "end": v(-81.11, 145.74) * mm});
            skLineSegment(sketch, "E750", {"start": v(-81.11, 145.74) * mm, "end": v(-81.16, 144.96) * mm});
            skLineSegment(sketch, "E751", {"start": v(-81.16, 144.96) * mm, "end": v(-81.18, 144.25) * mm});
            skLineSegment(sketch, "E752", {"start": v(-81.18, 144.25) * mm, "end": v(-81.18, 143.69) * mm});
            skLineSegment(sketch, "E753", {"start": v(-81.18, 143.69) * mm, "end": v(-81.16, 132.6) * mm});
            skLineSegment(sketch, "E754", {"start": v(-81.16, 132.6) * mm, "end": v(-81.16, 115.7) * mm});
            skLineSegment(sketch, "E755", {"start": v(-81.16, 115.7) * mm, "end": v(-81.21, 114.42) * mm});
            skLineSegment(sketch, "E756", {"start": v(-81.21, 114.42) * mm, "end": v(-81.34, 109.98) * mm});
            skLineSegment(sketch, "E757", {"start": v(-81.34, 109.98) * mm, "end": v(-81.43, 105.34) * mm});
            skLineSegment(sketch, "E758", {"start": v(-81.43, 105.34) * mm, "end": v(-81.56, 100.55) * mm});
            skLineSegment(sketch, "E759", {"start": v(-81.56, 100.55) * mm, "end": v(-81.83, 95.64) * mm});
            skLineSegment(sketch, "E760", {"start": v(-81.83, 95.64) * mm, "end": v(-82.34, 90.67) * mm});
            skLineSegment(sketch, "E761", {"start": v(-82.34, 90.67) * mm, "end": v(-83.18, 85.68) * mm});
            skLineSegment(sketch, "E762", {"start": v(-83.18, 85.68) * mm, "end": v(-84.45, 80.7) * mm});
            skLineSegment(sketch, "E763", {"start": v(-84.45, 80.7) * mm, "end": v(-86.23, 75.8) * mm});
            skLineSegment(sketch, "E764", {"start": v(-86.23, 75.8) * mm, "end": v(-120.84, -5.5) * mm});
            skLineSegment(sketch, "E765", {"start": v(-120.84, -5.5) * mm, "end": v(-122.7, -7.7) * mm});
            skLineSegment(sketch, "E766", {"start": v(-122.7, -7.7) * mm, "end": v(-126.47, -10.74) * mm});
            skLineSegment(sketch, "E767", {"start": v(-126.47, -10.74) * mm, "end": v(-131.62, -14.34) * mm});
            skLineSegment(sketch, "E768", {"start": v(-131.62, -14.34) * mm, "end": v(-137.62, -18.25) * mm});
            skLineSegment(sketch, "E769", {"start": v(-137.62, -18.25) * mm, "end": v(-143.94, -22.21) * mm});
            skLineSegment(sketch, "E770", {"start": v(-143.94, -22.21) * mm, "end": v(-150.04, -25.95) * mm});
            skLineSegment(sketch, "E771", {"start": v(-150.04, -25.95) * mm, "end": v(-155.39, -29.2) * mm});
            skLineSegment(sketch, "E772", {"start": v(-155.39, -29.2) * mm, "end": v(-159.45, -31.7) * mm});
            skLineSegment(sketch, "E773", {"start": v(-159.45, -31.7) * mm, "end": v(-164.8, -35.6) * mm});
            skLineSegment(sketch, "E774", {"start": v(-164.8, -35.6) * mm, "end": v(-168.85, -40.17) * mm});
            skLineSegment(sketch, "E775", {"start": v(-168.85, -40.17) * mm, "end": v(-171.77, -45.18) * mm});
            skLineSegment(sketch, "E776", {"start": v(-171.77, -45.18) * mm, "end": v(-173.75, -50.43) * mm});
            skLineSegment(sketch, "E777", {"start": v(-173.75, -50.43) * mm, "end": v(-174.97, -55.7) * mm});
            skLineSegment(sketch, "E778", {"start": v(-174.97, -55.7) * mm, "end": v(-175.62, -60.79) * mm});
            skLineSegment(sketch, "E779", {"start": v(-175.62, -60.79) * mm, "end": v(-175.87, -65.46) * mm});
            skLineSegment(sketch, "E780", {"start": v(-175.87, -65.46) * mm, "end": v(-175.91, -69.5) * mm});
            skLineSegment(sketch, "E781", {"start": v(-175.91, -69.5) * mm, "end": v(-175.91, -215.15) * mm});
            skLineSegment(sketch, "E782", {"start": v(-175.91, -215.15) * mm, "end": v(-173.77, -224.36) * mm});
            skLineSegment(sketch, "E783", {"start": v(-173.77, -224.36) * mm, "end": v(-169.93, -231.65) * mm});
            skLineSegment(sketch, "E784", {"start": v(-169.93, -231.65) * mm, "end": v(-164.92, -237.23) * mm});
            skLineSegment(sketch, "E785", {"start": v(-164.92, -237.23) * mm, "end": v(-159.28, -241.32) * mm});
            skLineSegment(sketch, "E786", {"start": v(-159.28, -241.32) * mm, "end": v(-153.52, -244.14) * mm});
            skLineSegment(sketch, "E787", {"start": v(-153.52, -244.14) * mm, "end": v(-148.18, -245.88) * mm});
            skLineSegment(sketch, "E788", {"start": v(-148.18, -245.88) * mm, "end": v(-143.78, -246.77) * mm});
            skLineSegment(sketch, "E789", {"start": v(-143.78, -246.77) * mm, "end": v(-140.86, -247.02) * mm});
            skLineSegment(sketch, "E790", {"start": v(-140.86, -247.02) * mm, "end": v(137.75, -247.02) * mm});
            skLineSegment(sketch, "E791", {"start": v(-118.7, 420.26) * mm, "end": v(-122.94, 419.84) * mm});
            skLineSegment(sketch, "E792", {"start": v(-122.94, 419.84) * mm, "end": v(-127.08, 418.63) * mm});
            skLineSegment(sketch, "E793", {"start": v(-127.08, 418.63) * mm, "end": v(-130.96, 416.7) * mm});
            skLineSegment(sketch, "E794", {"start": v(-130.96, 416.7) * mm, "end": v(-134.42, 414.13) * mm});
            skLineSegment(sketch, "E795", {"start": v(-134.42, 414.13) * mm, "end": v(-137.3, 411) * mm});
            skLineSegment(sketch, "E796", {"start": v(-137.3, 411) * mm, "end": v(-139.46, 407.37) * mm});
            skLineSegment(sketch, "E797", {"start": v(-139.46, 407.37) * mm, "end": v(-140.7, 403.32) * mm});
            skLineSegment(sketch, "E798", {"start": v(-140.7, 403.32) * mm, "end": v(-140.9, 398.93) * mm});
            skLineSegment(sketch, "E799", {"start": v(-140.9, 398.93) * mm, "end": v(-129.32, 261.5) * mm});
            skLineSegment(sketch, "E800", {"start": v(-129.32, 261.5) * mm, "end": v(-128.6, 257.06) * mm});
            skLineSegment(sketch, "E801", {"start": v(-128.6, 257.06) * mm, "end": v(-127.22, 252.83) * mm});
            skLineSegment(sketch, "E802", {"start": v(-127.22, 252.83) * mm, "end": v(-125.22, 248.94) * mm});
            skLineSegment(sketch, "E803", {"start": v(-125.22, 248.94) * mm, "end": v(-122.63, 245.49) * mm});
            skLineSegment(sketch, "E804", {"start": v(-122.63, 245.49) * mm, "end": v(-119.48, 242.6) * mm});
            skLineSegment(sketch, "E805", {"start": v(-119.48, 242.6) * mm, "end": v(-115.83, 240.4) * mm});
            skLineSegment(sketch, "E806", {"start": v(-115.83, 240.4) * mm, "end": v(-111.7, 238.99) * mm});
            skLineSegment(sketch, "E807", {"start": v(-111.7, 238.99) * mm, "end": v(-107.12, 238.5) * mm});
            skLineSegment(sketch, "E808", {"start": v(-107.12, 238.5) * mm, "end": v(104, 238.5) * mm});
            skLineSegment(sketch, "E809", {"start": v(104, 238.5) * mm, "end": v(108.57, 238.99) * mm});
            skLineSegment(sketch, "E810", {"start": v(108.57, 238.99) * mm, "end": v(112.7, 240.4) * mm});
            skLineSegment(sketch, "E811", {"start": v(112.7, 240.4) * mm, "end": v(116.36, 242.6) * mm});
            skLineSegment(sketch, "E812", {"start": v(116.36, 242.6) * mm, "end": v(119.5, 245.49) * mm});
            skLineSegment(sketch, "E813", {"start": v(119.5, 245.49) * mm, "end": v(122.1, 248.94) * mm});
            skLineSegment(sketch, "E814", {"start": v(122.1, 248.94) * mm, "end": v(124.1, 252.83) * mm});
            skLineSegment(sketch, "E815", {"start": v(124.1, 252.83) * mm, "end": v(125.48, 257.06) * mm});
            skLineSegment(sketch, "E816", {"start": v(125.48, 257.06) * mm, "end": v(126.2, 261.5) * mm});
            skLineSegment(sketch, "E817", {"start": v(126.2, 261.5) * mm, "end": v(137.78, 398.93) * mm});
            skLineSegment(sketch, "E818", {"start": v(137.78, 398.93) * mm, "end": v(137.59, 403.32) * mm});
            skLineSegment(sketch, "E819", {"start": v(137.59, 403.32) * mm, "end": v(136.33, 407.37) * mm});
            skLineSegment(sketch, "E820", {"start": v(136.33, 407.37) * mm, "end": v(134.19, 411) * mm});
            skLineSegment(sketch, "E821", {"start": v(134.19, 411) * mm, "end": v(131.3, 414.13) * mm});
            skLineSegment(sketch, "E822", {"start": v(131.3, 414.13) * mm, "end": v(127.84, 416.7) * mm});
            skLineSegment(sketch, "E823", {"start": v(127.84, 416.7) * mm, "end": v(123.96, 418.63) * mm});
            skLineSegment(sketch, "E824", {"start": v(123.96, 418.63) * mm, "end": v(119.82, 419.84) * mm});
            skLineSegment(sketch, "E825", {"start": v(119.82, 419.84) * mm, "end": v(115.58, 420.26) * mm});
            skLineSegment(sketch, "E826", {"start": v(115.58, 420.26) * mm, "end": v(-118.7, 420.26) * mm});
            skSolve(sketch);
        }
        {
            var Q0;
            Q0=makeQuery(id+"F0.imprint","IMPRINT",FACE,{"disambiguationData":[TD([[makeQuery(id+"F0.imprint","IMPRINT",EDGE,{"derivedFrom":sQuery(id+"F0.wireOp",EDGE,"E0")}),1.0]])]});
            var Q1;
            Q1=makeQuery(id+"F0.imprint","IMPRINT",FACE,{"disambiguationData":[TD([[makeQuery(id+"F0.imprint","IMPRINT",EDGE,{"derivedFrom":sQuery(id+"F0.wireOp",EDGE,"E77")}),-1.0]])]});
            var Q2;
            {var subQ10=sQuery(id+"F0.wireOp",EDGE,"E495");Q2=makeQuery(id+"F0.imprint","IMPRINT",FACE,{"disambiguationData":[TD([[makeQuery(id+"F0.imprint","IMPRINT",EDGE,{"derivedFrom":subQ10}),-1.0]])]});}
            var Q3;
            Q3=makeQuery(id+"F0.imprint","IMPRINT",FACE,{"disambiguationData":[TD([[makeQuery(id+"F0.imprint","IMPRINT",EDGE,{"derivedFrom":sQuery(id+"F0.wireOp",EDGE,"E334")}),1.0]])]});
            var Q4;
            {var subQ4=sQuery(id+"F0.wireOp",EDGE,"E67");Q4=makeQuery(id+"F0.imprint","IMPRINT",FACE,{"disambiguationData":[TD([[makeQuery(id+"F0.imprint","IMPRINT",EDGE,{"derivedFrom":subQ4}),-1.0]])]});}
            var Q5;
            Q5=makeQuery(id+"F0.imprint","IMPRINT",FACE,{"disambiguationData":[TD([[makeQuery(id+"F0.imprint","IMPRINT",EDGE,{"derivedFrom":sQuery(id+"F0.wireOp",EDGE,"E791")}),1.0]])]});
            var Q6;
            Q6=makeQuery(id+"F0.imprint","IMPRINT",FACE,{"disambiguationData":[TD([[makeQuery(id+"F0.imprint","IMPRINT",EDGE,{"derivedFrom":sQuery(id+"F0.wireOp",EDGE,"E705")}),1.0]])]});
            extrude(context, id + "F1", {"entities" : qUnion([Q0, Q1, Q2, Q3, Q4, Q5, Q6]), "depth" : 20 * mm, "offsetDistance" : 25 * mm});
        }
        {
            var Q0;
            Q0=qCreatedBy(makeId("Right.planeOp"),FACE);
            var sketch = newSketch(context, id + "F2", { "sketchPlane" : qUnion([Q0])});
            skCircle(sketch, "E827", {"center": v(-10.2, 131.71) * mm, "radius": 5 * mm});
            skSolve(sketch);
        }
        {
            var Q0;
            Q0 = qSketchRegion(id + "F2", true);
            extrude(context, id + "F3", {"entities" : qUnion([Q0]), "operationType" : NewBodyOperationType.REMOVE, "endBound" : BoundingType.SYMMETRIC, "oppositeDirection" : true, "depth" : 276 * mm, "offsetDistance" : 25 * mm});
        }
        {
            var Q0;
            Q0=qCreatedBy(makeId("Right.planeOp"),FACE);
            cPlane(context, id + "F4", {"entities" : qUnion([Q0]), "cplaneType" : CPlaneType.OFFSET, "offset" : 84 * mm, "width" : 150 * mm, "height" : 150 * mm});
        }
        {
            var Q0;
            Q0=qCreatedBy(makeId("Right.planeOp"),FACE);
            cPlane(context, id + "F5", {"entities" : qUnion([Q0]), "cplaneType" : CPlaneType.OFFSET, "offset" : 87 * mm, "oppositeDirection" : true, "width" : 150 * mm, "height" : 150 * mm});
        }
        {
            var Q0;
            Q0=qCreatedBy(id+"F4.planeOp",FACE);
            var sketch = newSketch(context, id + "F6", { "sketchPlane" : qUnion([Q0])});
            skCircle(sketch, "E828.0", {"center": v(-10.2, 131.71) * mm, "radius": 4.83 * mm});
            skSolve(sketch);
        }
        {
            var Q0;
            Q0=qCreatedBy(id+"F5.planeOp",FACE);
            var sketch = newSketch(context, id + "F7", { "sketchPlane" : qUnion([Q0])});
            skCircle(sketch, "E829.0.0", {"center": v(-10.2, 131.71) * mm, "radius": 4.83 * mm});
            skSolve(sketch);
        }
        {
            var Q0;
            Q0=makeQuery(id+"F7.imprint","IMPRINT",FACE,{"disambiguationData":[TD([[makeQuery(id+"F7.imprint","IMPRINT",EDGE,{"derivedFrom":sQuery(id+"F7.wireOp",EDGE,"E829.0.0")}),1.0]])]});
            var Q1;
            Q1=makeQuery(id+"F6.imprint","IMPRINT",FACE,{"disambiguationData":[TD([[makeQuery(id+"F6.imprint","IMPRINT",EDGE,{"derivedFrom":sQuery(id+"F6.wireOp",EDGE,"E828.0")}),1.0]])]});
            extrude(context, id + "F8", {"entities" : qUnion([Q0, Q1]), "endBound" : BoundingType.SYMMETRIC, "depth" : 40 * mm, "offsetDistance" : 25 * mm});
        }
    });
